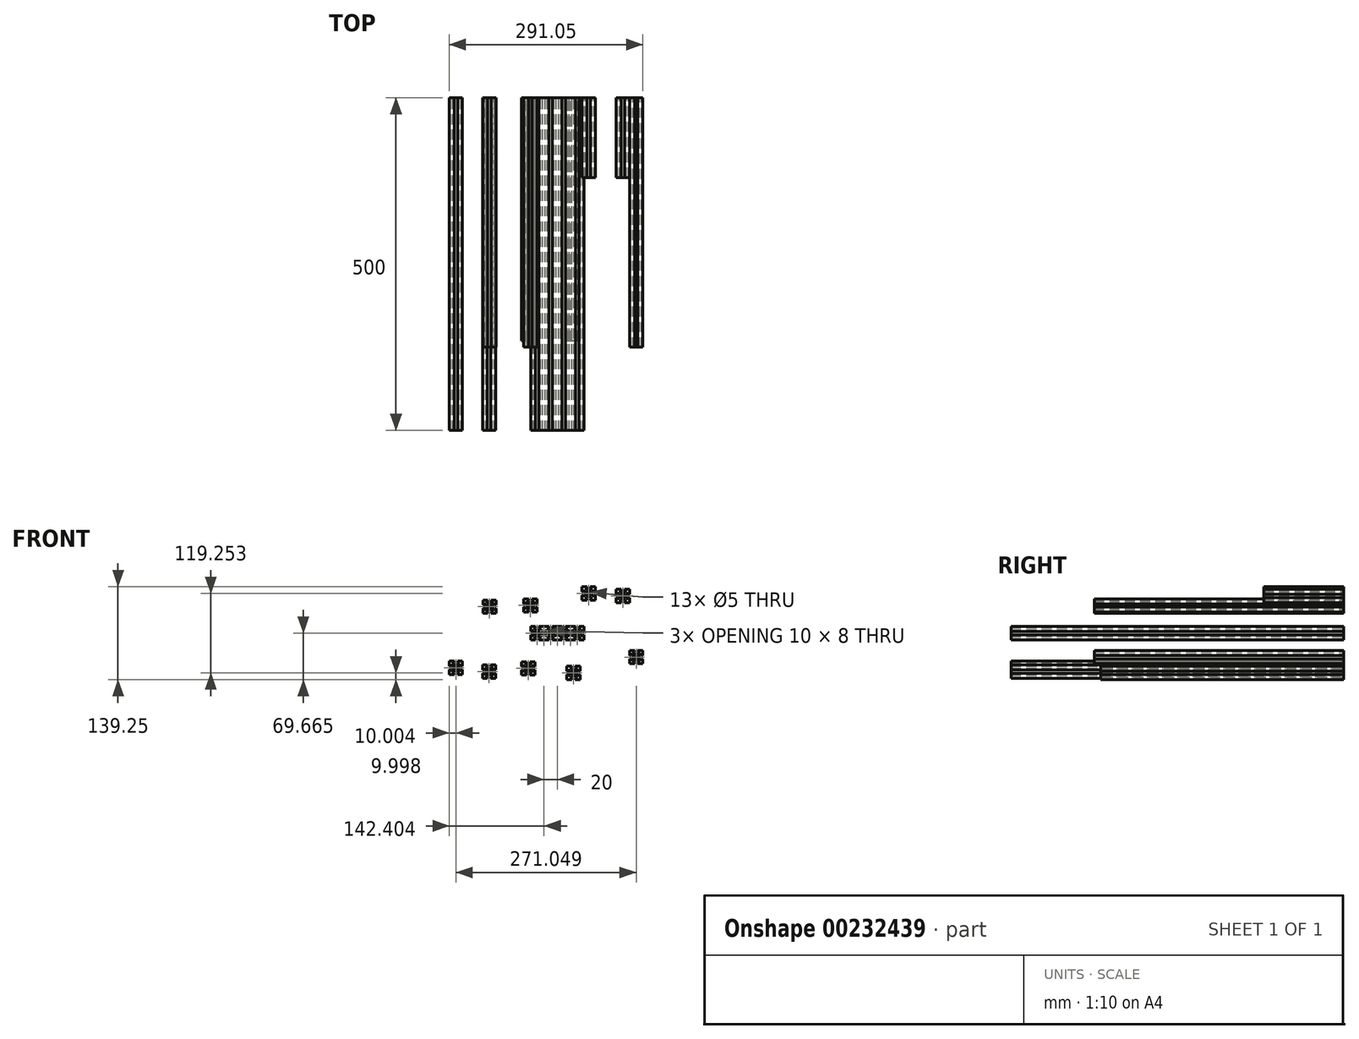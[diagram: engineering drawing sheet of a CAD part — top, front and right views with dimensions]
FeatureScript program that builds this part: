
annotation { "Feature Type Name" : "Feature", "Feature Type Description" : "" }
export const myFeature = defineFeature(function(context is Context, id is Id, definition is map)
    precondition{}
    {
        {
            var Q0;
            Q0=qCreatedBy(makeId("Front.planeOp"),FACE);
            var sketch = newSketch(context, id + "F0", { "sketchPlane" : qUnion([Q0])});
            skLineSegment(sketch, "E0.bottom", {"start": v(-60.37, 62.95) * mm, "end": v(-52.87, 62.95) * mm});
            skLineSegment(sketch, "E0.top", {"start": v(-60.37, 42.95) * mm, "end": v(-52.87, 42.95) * mm});
            skLineSegment(sketch, "E0.left", {"start": v(-60.37, 62.95) * mm, "end": v(-60.37, 55.45) * mm});
            skLineSegment(sketch, "E0.right", {"start": v(-40.37, 62.95) * mm, "end": v(-40.37, 55.45) * mm});
            skLineSegment(sketch, "E1.right", {"start": v(-47.87, 62.95) * mm, "end": v(-47.87, 60.95) * mm});
            skCircle(sketch, "E2", {"center": v(-50.37, 52.95) * mm, "radius": 2.5 * mm});
            skLineSegment(sketch, "E3.MirrorCS", {"start": v(-52.87, 62.95) * mm, "end": v(-52.87, 60.95) * mm});
            skLineSegment(sketch, "E4.bottom", {"start": v(-47.87, 60.95) * mm, "end": v(-46.37, 60.95) * mm});
            skLineSegment(sketch, "E4.top", {"start": v(-50.37, 57.95) * mm, "end": v(-46.37, 57.95) * mm});
            skLineSegment(sketch, "E4.right", {"start": v(-46.37, 60.95) * mm, "end": v(-46.37, 57.95) * mm});
            skLineSegment(sketch, "E5.MirrorCS", {"start": v(-54.37, 60.95) * mm, "end": v(-54.37, 57.95) * mm});
            skLineSegment(sketch, "E6.MirrorCS", {"start": v(-52.87, 60.95) * mm, "end": v(-54.37, 60.95) * mm});
            skLineSegment(sketch, "E7.MirrorCS", {"start": v(-50.37, 57.95) * mm, "end": v(-54.37, 57.95) * mm});
            skPoint(sketch, "E8.MirrorCS.end.orphan", {"position": v(-52.87, 60.95) * mm});
            skPoint(sketch, "E8.MirrorCS.start.orphan", {"position": v(-50.37, 60.95) * mm});
            skLineSegment(sketch, "E9.trimOffspring", {"start": v(-47.87, 62.95) * mm, "end": v(-40.37, 62.95) * mm});
            skPoint(sketch, "E1.bottom.start.orphan", {"position": v(-50.37, 62.95) * mm});
            skLineSegment(sketch, "E10.MirrorCS", {"start": v(-58.37, 55.45) * mm, "end": v(-58.37, 56.95) * mm});
            skLineSegment(sketch, "E11.MirrorCS", {"start": v(-55.37, 52.95) * mm, "end": v(-55.37, 56.95) * mm});
            skLineSegment(sketch, "E12.MirrorCS", {"start": v(-58.37, 48.95) * mm, "end": v(-55.37, 48.95) * mm});
            skLineSegment(sketch, "E13.MirrorCS", {"start": v(-55.37, 52.95) * mm, "end": v(-55.37, 48.95) * mm});
            skLineSegment(sketch, "E14.MirrorCS", {"start": v(-58.37, 50.45) * mm, "end": v(-58.37, 48.95) * mm});
            skLineSegment(sketch, "E15.MirrorCS", {"start": v(-58.37, 56.95) * mm, "end": v(-55.37, 56.95) * mm});
            skPoint(sketch, "E16.MirrorP", {"position": v(-58.37, 55.45) * mm});
            skPoint(sketch, "E17.MirrorP", {"position": v(-60.37, 52.95) * mm});
            skLineSegment(sketch, "E18.MirrorCS", {"start": v(-60.37, 55.45) * mm, "end": v(-58.37, 55.45) * mm});
            skLineSegment(sketch, "E19.MirrorCS", {"start": v(-60.37, 50.45) * mm, "end": v(-58.37, 50.45) * mm});
            skPoint(sketch, "E20.MirrorP", {"position": v(-58.37, 52.95) * mm});
            skPoint(sketch, "E21.orphan", {"position": v(-40.37, 62.95) * mm});
            skPoint(sketch, "E22.MirrorP", {"position": v(-40.37, 52.95) * mm});
            skLineSegment(sketch, "E23.MirrorCS", {"start": v(-42.37, 50.45) * mm, "end": v(-42.37, 48.95) * mm});
            skLineSegment(sketch, "E24.MirrorCS", {"start": v(-45.37, 52.95) * mm, "end": v(-45.37, 48.95) * mm});
            skLineSegment(sketch, "E25.MirrorCS", {"start": v(-40.37, 50.45) * mm, "end": v(-42.37, 50.45) * mm});
            skLineSegment(sketch, "E26.MirrorCS", {"start": v(-42.37, 55.45) * mm, "end": v(-42.37, 56.95) * mm});
            skLineSegment(sketch, "E27.MirrorCS", {"start": v(-45.37, 52.95) * mm, "end": v(-45.37, 56.95) * mm});
            skPoint(sketch, "E28.MirrorP", {"position": v(-42.37, 52.95) * mm});
            skLineSegment(sketch, "E29.MirrorCS", {"start": v(-42.37, 56.95) * mm, "end": v(-45.37, 56.95) * mm});
            skLineSegment(sketch, "E30.MirrorCS", {"start": v(-40.37, 55.45) * mm, "end": v(-42.37, 55.45) * mm});
            skLineSegment(sketch, "E31.MirrorCS", {"start": v(-42.37, 48.95) * mm, "end": v(-45.37, 48.95) * mm});
            skPoint(sketch, "E32.MirrorP", {"position": v(-42.37, 50.45) * mm});
            skLineSegment(sketch, "E33.MirrorCS", {"start": v(-47.87, 44.95) * mm, "end": v(-46.37, 44.95) * mm});
            skLineSegment(sketch, "E34.MirrorCS", {"start": v(-47.87, 42.95) * mm, "end": v(-47.87, 44.95) * mm});
            skLineSegment(sketch, "E35.MirrorCS", {"start": v(-52.87, 42.95) * mm, "end": v(-52.87, 44.95) * mm});
            skLineSegment(sketch, "E36.MirrorCS", {"start": v(-52.87, 44.95) * mm, "end": v(-54.37, 44.95) * mm});
            skLineSegment(sketch, "E37.MirrorCS", {"start": v(-54.37, 44.95) * mm, "end": v(-54.37, 47.95) * mm});
            skLineSegment(sketch, "E38.MirrorCS", {"start": v(-50.37, 47.95) * mm, "end": v(-54.37, 47.95) * mm});
            skLineSegment(sketch, "E39.MirrorCS", {"start": v(-46.37, 44.95) * mm, "end": v(-46.37, 47.95) * mm});
            skLineSegment(sketch, "E40.MirrorCS", {"start": v(-50.37, 47.95) * mm, "end": v(-46.37, 47.95) * mm});
            skLineSegment(sketch, "E41.trimOffspring", {"start": v(-40.37, 50.45) * mm, "end": v(-40.37, 42.95) * mm});
            skLineSegment(sketch, "E42.trimOffspring", {"start": v(-47.87, 42.95) * mm, "end": v(-40.37, 42.95) * mm});
            skLineSegment(sketch, "E43.trimOffspring", {"start": v(-60.37, 50.45) * mm, "end": v(-60.37, 42.95) * mm});
            skPoint(sketch, "E44.orphan", {"position": v(-60.37, 42.95) * mm});
            skLineSegment(sketch, "E45.bottom", {"start": v(1.09, 64.79) * mm, "end": v(8.59, 64.79) * mm});
            skLineSegment(sketch, "E45.top", {"start": v(1.09, 44.79) * mm, "end": v(8.59, 44.79) * mm});
            skLineSegment(sketch, "E45.left", {"start": v(1.09, 64.79) * mm, "end": v(1.09, 57.29) * mm});
            skLineSegment(sketch, "E45.right", {"start": v(21.09, 64.79) * mm, "end": v(21.09, 57.29) * mm});
            skLineSegment(sketch, "E46.right", {"start": v(13.59, 64.79) * mm, "end": v(13.59, 62.79) * mm});
            skCircle(sketch, "E47", {"center": v(11.09, 54.79) * mm, "radius": 2.5 * mm});
            skLineSegment(sketch, "E48.MirrorCS", {"start": v(8.59, 64.79) * mm, "end": v(8.59, 62.79) * mm});
            skLineSegment(sketch, "E49.bottom", {"start": v(13.59, 62.79) * mm, "end": v(15.09, 62.79) * mm});
            skLineSegment(sketch, "E49.top", {"start": v(11.09, 59.79) * mm, "end": v(15.09, 59.79) * mm});
            skLineSegment(sketch, "E49.right", {"start": v(15.09, 62.79) * mm, "end": v(15.09, 59.79) * mm});
            skLineSegment(sketch, "E50.MirrorCS", {"start": v(7.09, 62.79) * mm, "end": v(7.09, 59.79) * mm});
            skLineSegment(sketch, "E51.MirrorCS", {"start": v(8.59, 62.79) * mm, "end": v(7.09, 62.79) * mm});
            skLineSegment(sketch, "E52.MirrorCS", {"start": v(11.09, 59.79) * mm, "end": v(7.09, 59.79) * mm});
            skPoint(sketch, "E53.MirrorCS.end.orphan", {"position": v(8.59, 62.79) * mm});
            skPoint(sketch, "E53.MirrorCS.start.orphan", {"position": v(11.09, 62.79) * mm});
            skLineSegment(sketch, "E54.trimOffspring", {"start": v(13.59, 64.79) * mm, "end": v(21.09, 64.79) * mm});
            skPoint(sketch, "E46.bottom.start.orphan", {"position": v(11.09, 64.79) * mm});
            skLineSegment(sketch, "E55.MirrorCS", {"start": v(3.09, 57.29) * mm, "end": v(3.09, 58.79) * mm});
            skLineSegment(sketch, "E56.MirrorCS", {"start": v(6.09, 54.79) * mm, "end": v(6.09, 58.79) * mm});
            skLineSegment(sketch, "E57.MirrorCS", {"start": v(3.09, 50.79) * mm, "end": v(6.09, 50.79) * mm});
            skLineSegment(sketch, "E58.MirrorCS", {"start": v(6.09, 54.79) * mm, "end": v(6.09, 50.79) * mm});
            skLineSegment(sketch, "E59.MirrorCS", {"start": v(3.09, 52.29) * mm, "end": v(3.09, 50.79) * mm});
            skLineSegment(sketch, "E60.MirrorCS", {"start": v(3.09, 58.79) * mm, "end": v(6.09, 58.79) * mm});
            skPoint(sketch, "E61.MirrorP", {"position": v(3.09, 57.29) * mm});
            skPoint(sketch, "E62.MirrorP", {"position": v(1.09, 54.79) * mm});
            skLineSegment(sketch, "E63.MirrorCS", {"start": v(1.09, 57.29) * mm, "end": v(3.09, 57.29) * mm});
            skLineSegment(sketch, "E64.MirrorCS", {"start": v(1.09, 52.29) * mm, "end": v(3.09, 52.29) * mm});
            skPoint(sketch, "E65.MirrorP", {"position": v(3.09, 54.79) * mm});
            skPoint(sketch, "E66.orphan", {"position": v(21.09, 64.79) * mm});
            skPoint(sketch, "E67.MirrorP", {"position": v(21.09, 54.79) * mm});
            skLineSegment(sketch, "E68.MirrorCS", {"start": v(19.09, 52.29) * mm, "end": v(19.09, 50.79) * mm});
            skLineSegment(sketch, "E69.MirrorCS", {"start": v(16.09, 54.79) * mm, "end": v(16.09, 50.79) * mm});
            skLineSegment(sketch, "E70.MirrorCS", {"start": v(21.09, 52.29) * mm, "end": v(19.09, 52.29) * mm});
            skLineSegment(sketch, "E71.MirrorCS", {"start": v(19.09, 57.29) * mm, "end": v(19.09, 58.79) * mm});
            skLineSegment(sketch, "E72.MirrorCS", {"start": v(16.09, 54.79) * mm, "end": v(16.09, 58.79) * mm});
            skPoint(sketch, "E73.MirrorP", {"position": v(19.09, 54.79) * mm});
            skLineSegment(sketch, "E74.MirrorCS", {"start": v(19.09, 58.79) * mm, "end": v(16.09, 58.79) * mm});
            skLineSegment(sketch, "E75.MirrorCS", {"start": v(21.09, 57.29) * mm, "end": v(19.09, 57.29) * mm});
            skLineSegment(sketch, "E76.MirrorCS", {"start": v(19.09, 50.79) * mm, "end": v(16.09, 50.79) * mm});
            skPoint(sketch, "E77.MirrorP", {"position": v(19.09, 52.29) * mm});
            skLineSegment(sketch, "E78.MirrorCS", {"start": v(13.59, 46.79) * mm, "end": v(15.09, 46.79) * mm});
            skLineSegment(sketch, "E79.MirrorCS", {"start": v(13.59, 44.79) * mm, "end": v(13.59, 46.79) * mm});
            skLineSegment(sketch, "E80.MirrorCS", {"start": v(8.59, 44.79) * mm, "end": v(8.59, 46.79) * mm});
            skLineSegment(sketch, "E81.MirrorCS", {"start": v(8.59, 46.79) * mm, "end": v(7.09, 46.79) * mm});
            skLineSegment(sketch, "E82.MirrorCS", {"start": v(7.09, 46.79) * mm, "end": v(7.09, 49.79) * mm});
            skLineSegment(sketch, "E83.MirrorCS", {"start": v(11.09, 49.79) * mm, "end": v(7.09, 49.79) * mm});
            skLineSegment(sketch, "E84.MirrorCS", {"start": v(15.09, 46.79) * mm, "end": v(15.09, 49.79) * mm});
            skLineSegment(sketch, "E85.MirrorCS", {"start": v(11.09, 49.79) * mm, "end": v(15.09, 49.79) * mm});
            skLineSegment(sketch, "E86.trimOffspring", {"start": v(21.09, 52.29) * mm, "end": v(21.09, 44.79) * mm});
            skLineSegment(sketch, "E87.trimOffspring", {"start": v(13.59, 44.79) * mm, "end": v(21.09, 44.79) * mm});
            skLineSegment(sketch, "E88.trimOffspring", {"start": v(1.09, 52.29) * mm, "end": v(1.09, 44.79) * mm});
            skPoint(sketch, "E89.orphan", {"position": v(1.09, 44.79) * mm});
            skLineSegment(sketch, "E90.bottom", {"start": v(-47.85, -7.16) * mm, "end": v(-40.35, -7.16) * mm});
            skLineSegment(sketch, "E90.top", {"start": v(-47.85, -27.16) * mm, "end": v(-40.35, -27.16) * mm});
            skLineSegment(sketch, "E90.left", {"start": v(-47.85, -7.16) * mm, "end": v(-47.85, -14.66) * mm});
            skLineSegment(sketch, "E90.right", {"start": v(-27.85, -7.16) * mm, "end": v(-27.85, -14.66) * mm});
            skLineSegment(sketch, "E91.right", {"start": v(-35.35, -7.16) * mm, "end": v(-35.35, -9.16) * mm});
            skCircle(sketch, "E92", {"center": v(-37.85, -17.16) * mm, "radius": 2.5 * mm});
            skLineSegment(sketch, "E93.MirrorCS", {"start": v(-40.35, -7.16) * mm, "end": v(-40.35, -9.16) * mm});
            skLineSegment(sketch, "E94.bottom", {"start": v(-35.35, -9.16) * mm, "end": v(-33.85, -9.16) * mm});
            skLineSegment(sketch, "E94.top", {"start": v(-37.85, -12.16) * mm, "end": v(-33.85, -12.16) * mm});
            skLineSegment(sketch, "E94.right", {"start": v(-33.85, -9.16) * mm, "end": v(-33.85, -12.16) * mm});
            skLineSegment(sketch, "E95.MirrorCS", {"start": v(-41.85, -9.16) * mm, "end": v(-41.85, -12.16) * mm});
            skLineSegment(sketch, "E96.MirrorCS", {"start": v(-40.35, -9.16) * mm, "end": v(-41.85, -9.16) * mm});
            skLineSegment(sketch, "E97.MirrorCS", {"start": v(-37.85, -12.16) * mm, "end": v(-41.85, -12.16) * mm});
            skPoint(sketch, "E98.MirrorCS.end.orphan", {"position": v(-40.35, -9.16) * mm});
            skPoint(sketch, "E98.MirrorCS.start.orphan", {"position": v(-37.85, -9.16) * mm});
            skLineSegment(sketch, "E99.trimOffspring", {"start": v(-35.35, -7.16) * mm, "end": v(-27.85, -7.16) * mm});
            skPoint(sketch, "E91.bottom.start.orphan", {"position": v(-37.85, -7.16) * mm});
            skLineSegment(sketch, "E100.MirrorCS", {"start": v(-45.85, -14.66) * mm, "end": v(-45.85, -13.16) * mm});
            skLineSegment(sketch, "E101.MirrorCS", {"start": v(-42.85, -17.16) * mm, "end": v(-42.85, -13.16) * mm});
            skLineSegment(sketch, "E102.MirrorCS", {"start": v(-45.85, -21.16) * mm, "end": v(-42.85, -21.16) * mm});
            skLineSegment(sketch, "E103.MirrorCS", {"start": v(-42.85, -17.16) * mm, "end": v(-42.85, -21.16) * mm});
            skLineSegment(sketch, "E104.MirrorCS", {"start": v(-45.85, -19.66) * mm, "end": v(-45.85, -21.16) * mm});
            skLineSegment(sketch, "E105.MirrorCS", {"start": v(-45.85, -13.16) * mm, "end": v(-42.85, -13.16) * mm});
            skPoint(sketch, "E106.MirrorP", {"position": v(-45.85, -14.66) * mm});
            skPoint(sketch, "E107.MirrorP", {"position": v(-47.85, -17.16) * mm});
            skLineSegment(sketch, "E108.MirrorCS", {"start": v(-47.85, -14.66) * mm, "end": v(-45.85, -14.66) * mm});
            skLineSegment(sketch, "E109.MirrorCS", {"start": v(-47.85, -19.66) * mm, "end": v(-45.85, -19.66) * mm});
            skPoint(sketch, "E110.MirrorP", {"position": v(-45.85, -17.16) * mm});
            skPoint(sketch, "E111.orphan", {"position": v(-27.85, -7.16) * mm});
            skPoint(sketch, "E112.MirrorP", {"position": v(-27.85, -17.16) * mm});
            skLineSegment(sketch, "E113.MirrorCS", {"start": v(-29.85, -19.66) * mm, "end": v(-29.85, -21.16) * mm});
            skLineSegment(sketch, "E114.MirrorCS", {"start": v(-32.85, -17.16) * mm, "end": v(-32.85, -21.16) * mm});
            skLineSegment(sketch, "E115.MirrorCS", {"start": v(-27.85, -19.66) * mm, "end": v(-29.85, -19.66) * mm});
            skLineSegment(sketch, "E116.MirrorCS", {"start": v(-29.85, -14.66) * mm, "end": v(-29.85, -13.16) * mm});
            skLineSegment(sketch, "E117.MirrorCS", {"start": v(-32.85, -17.16) * mm, "end": v(-32.85, -13.16) * mm});
            skPoint(sketch, "E118.MirrorP", {"position": v(-29.85, -17.16) * mm});
            skLineSegment(sketch, "E119.MirrorCS", {"start": v(-29.85, -13.16) * mm, "end": v(-32.85, -13.16) * mm});
            skLineSegment(sketch, "E120.MirrorCS", {"start": v(-27.85, -14.66) * mm, "end": v(-29.85, -14.66) * mm});
            skLineSegment(sketch, "E121.MirrorCS", {"start": v(-29.85, -21.16) * mm, "end": v(-32.85, -21.16) * mm});
            skPoint(sketch, "E122.MirrorP", {"position": v(-29.85, -19.66) * mm});
            skLineSegment(sketch, "E123.MirrorCS", {"start": v(-35.35, -25.16) * mm, "end": v(-33.85, -25.16) * mm});
            skLineSegment(sketch, "E124.MirrorCS", {"start": v(-35.35, -27.16) * mm, "end": v(-35.35, -25.16) * mm});
            skLineSegment(sketch, "E125.MirrorCS", {"start": v(-40.35, -27.16) * mm, "end": v(-40.35, -25.16) * mm});
            skLineSegment(sketch, "E126.MirrorCS", {"start": v(-40.35, -25.16) * mm, "end": v(-41.85, -25.16) * mm});
            skLineSegment(sketch, "E127.MirrorCS", {"start": v(-41.85, -25.16) * mm, "end": v(-41.85, -22.16) * mm});
            skLineSegment(sketch, "E128.MirrorCS", {"start": v(-37.85, -22.16) * mm, "end": v(-41.85, -22.16) * mm});
            skLineSegment(sketch, "E129.MirrorCS", {"start": v(-33.85, -25.16) * mm, "end": v(-33.85, -22.16) * mm});
            skLineSegment(sketch, "E130.MirrorCS", {"start": v(-37.85, -22.16) * mm, "end": v(-33.85, -22.16) * mm});
            skLineSegment(sketch, "E131.trimOffspring", {"start": v(-27.85, -19.66) * mm, "end": v(-27.85, -27.16) * mm});
            skLineSegment(sketch, "E132.trimOffspring", {"start": v(-35.35, -27.16) * mm, "end": v(-27.85, -27.16) * mm});
            skLineSegment(sketch, "E133.trimOffspring", {"start": v(-47.85, -19.66) * mm, "end": v(-47.85, -27.16) * mm});
            skPoint(sketch, "E134.orphan", {"position": v(-47.85, -27.16) * mm});
            skLineSegment(sketch, "E135.bottom", {"start": v(36.99, -2) * mm, "end": v(44.49, -2) * mm});
            skLineSegment(sketch, "E135.top", {"start": v(36.99, -22) * mm, "end": v(44.49, -22) * mm});
            skLineSegment(sketch, "E135.left", {"start": v(36.99, -2) * mm, "end": v(36.99, -9.5) * mm});
            skLineSegment(sketch, "E135.right", {"start": v(56.99, -2) * mm, "end": v(56.99, -9.5) * mm});
            skLineSegment(sketch, "E136.right", {"start": v(49.49, -2) * mm, "end": v(49.49, -4) * mm});
            skCircle(sketch, "E137", {"center": v(46.99, -12) * mm, "radius": 2.5 * mm});
            skLineSegment(sketch, "E138.MirrorCS", {"start": v(44.49, -2) * mm, "end": v(44.49, -4) * mm});
            skLineSegment(sketch, "E139.bottom", {"start": v(49.49, -4) * mm, "end": v(50.99, -4) * mm});
            skLineSegment(sketch, "E139.top", {"start": v(46.99, -7) * mm, "end": v(50.99, -7) * mm});
            skLineSegment(sketch, "E139.right", {"start": v(50.99, -4) * mm, "end": v(50.99, -7) * mm});
            skLineSegment(sketch, "E140.MirrorCS", {"start": v(42.99, -4) * mm, "end": v(42.99, -7) * mm});
            skLineSegment(sketch, "E141.MirrorCS", {"start": v(44.49, -4) * mm, "end": v(42.99, -4) * mm});
            skLineSegment(sketch, "E142.MirrorCS", {"start": v(46.99, -7) * mm, "end": v(42.99, -7) * mm});
            skPoint(sketch, "E143.MirrorCS.end.orphan", {"position": v(44.49, -4) * mm});
            skPoint(sketch, "E143.MirrorCS.start.orphan", {"position": v(46.99, -4) * mm});
            skLineSegment(sketch, "E144.trimOffspring", {"start": v(49.49, -2) * mm, "end": v(56.99, -2) * mm});
            skPoint(sketch, "E136.bottom.start.orphan", {"position": v(46.99, -2) * mm});
            skLineSegment(sketch, "E145.MirrorCS", {"start": v(38.99, -9.5) * mm, "end": v(38.99, -8) * mm});
            skLineSegment(sketch, "E146.MirrorCS", {"start": v(41.99, -12) * mm, "end": v(41.99, -8) * mm});
            skLineSegment(sketch, "E147.MirrorCS", {"start": v(38.99, -16) * mm, "end": v(41.99, -16) * mm});
            skLineSegment(sketch, "E148.MirrorCS", {"start": v(41.99, -12) * mm, "end": v(41.99, -16) * mm});
            skLineSegment(sketch, "E149.MirrorCS", {"start": v(38.99, -14.5) * mm, "end": v(38.99, -16) * mm});
            skLineSegment(sketch, "E150.MirrorCS", {"start": v(38.99, -8) * mm, "end": v(41.99, -8) * mm});
            skPoint(sketch, "E151.MirrorP", {"position": v(38.99, -9.5) * mm});
            skPoint(sketch, "E152.MirrorP", {"position": v(36.99, -12) * mm});
            skLineSegment(sketch, "E153.MirrorCS", {"start": v(36.99, -9.5) * mm, "end": v(38.99, -9.5) * mm});
            skLineSegment(sketch, "E154.MirrorCS", {"start": v(36.99, -14.5) * mm, "end": v(38.99, -14.5) * mm});
            skPoint(sketch, "E155.MirrorP", {"position": v(38.99, -12) * mm});
            skPoint(sketch, "E156.orphan", {"position": v(56.99, -2) * mm});
            skPoint(sketch, "E157.MirrorP", {"position": v(56.99, -12) * mm});
            skLineSegment(sketch, "E158.MirrorCS", {"start": v(54.99, -14.5) * mm, "end": v(54.99, -16) * mm});
            skLineSegment(sketch, "E159.MirrorCS", {"start": v(51.99, -12) * mm, "end": v(51.99, -16) * mm});
            skLineSegment(sketch, "E160.MirrorCS", {"start": v(56.99, -14.5) * mm, "end": v(54.99, -14.5) * mm});
            skLineSegment(sketch, "E161.MirrorCS", {"start": v(54.99, -9.5) * mm, "end": v(54.99, -8) * mm});
            skLineSegment(sketch, "E162.MirrorCS", {"start": v(51.99, -12) * mm, "end": v(51.99, -8) * mm});
            skPoint(sketch, "E163.MirrorP", {"position": v(54.99, -12) * mm});
            skLineSegment(sketch, "E164.MirrorCS", {"start": v(54.99, -8) * mm, "end": v(51.99, -8) * mm});
            skLineSegment(sketch, "E165.MirrorCS", {"start": v(56.99, -9.5) * mm, "end": v(54.99, -9.5) * mm});
            skLineSegment(sketch, "E166.MirrorCS", {"start": v(54.99, -16) * mm, "end": v(51.99, -16) * mm});
            skPoint(sketch, "E167.MirrorP", {"position": v(54.99, -14.5) * mm});
            skLineSegment(sketch, "E168.MirrorCS", {"start": v(49.49, -20) * mm, "end": v(50.99, -20) * mm});
            skLineSegment(sketch, "E169.MirrorCS", {"start": v(49.49, -22) * mm, "end": v(49.49, -20) * mm});
            skLineSegment(sketch, "E170.MirrorCS", {"start": v(44.49, -22) * mm, "end": v(44.49, -20) * mm});
            skLineSegment(sketch, "E171.MirrorCS", {"start": v(44.49, -20) * mm, "end": v(42.99, -20) * mm});
            skLineSegment(sketch, "E172.MirrorCS", {"start": v(42.99, -20) * mm, "end": v(42.99, -17) * mm});
            skLineSegment(sketch, "E173.MirrorCS", {"start": v(46.99, -17) * mm, "end": v(42.99, -17) * mm});
            skLineSegment(sketch, "E174.MirrorCS", {"start": v(50.99, -20) * mm, "end": v(50.99, -17) * mm});
            skLineSegment(sketch, "E175.MirrorCS", {"start": v(46.99, -17) * mm, "end": v(50.99, -17) * mm});
            skLineSegment(sketch, "E176.trimOffspring", {"start": v(56.99, -14.5) * mm, "end": v(56.99, -22) * mm});
            skLineSegment(sketch, "E177.trimOffspring", {"start": v(49.49, -22) * mm, "end": v(56.99, -22) * mm});
            skLineSegment(sketch, "E178.trimOffspring", {"start": v(36.99, -14.5) * mm, "end": v(36.99, -22) * mm});
            skPoint(sketch, "E179.orphan", {"position": v(36.99, -22) * mm});
            skLineSegment(sketch, "E180.bottom", {"start": v(61.03, 62.56) * mm, "end": v(68.53, 62.56) * mm});
            skLineSegment(sketch, "E180.top", {"start": v(61.03, 42.56) * mm, "end": v(68.53, 42.56) * mm});
            skLineSegment(sketch, "E180.left", {"start": v(61.03, 62.56) * mm, "end": v(61.03, 55.06) * mm});
            skLineSegment(sketch, "E180.right", {"start": v(81.03, 62.56) * mm, "end": v(81.03, 55.06) * mm});
            skLineSegment(sketch, "E181.right", {"start": v(73.53, 62.56) * mm, "end": v(73.53, 60.56) * mm});
            skCircle(sketch, "E182", {"center": v(71.03, 52.56) * mm, "radius": 2.5 * mm});
            skLineSegment(sketch, "E183.MirrorCS", {"start": v(68.53, 62.56) * mm, "end": v(68.53, 60.56) * mm});
            skLineSegment(sketch, "E184.bottom", {"start": v(73.53, 60.56) * mm, "end": v(75.03, 60.56) * mm});
            skLineSegment(sketch, "E184.top", {"start": v(71.03, 57.56) * mm, "end": v(75.03, 57.56) * mm});
            skLineSegment(sketch, "E184.right", {"start": v(75.03, 60.56) * mm, "end": v(75.03, 57.56) * mm});
            skLineSegment(sketch, "E185.MirrorCS", {"start": v(67.03, 60.56) * mm, "end": v(67.03, 57.56) * mm});
            skLineSegment(sketch, "E186.MirrorCS", {"start": v(68.53, 60.56) * mm, "end": v(67.03, 60.56) * mm});
            skLineSegment(sketch, "E187.MirrorCS", {"start": v(71.03, 57.56) * mm, "end": v(67.03, 57.56) * mm});
            skPoint(sketch, "E188.MirrorCS.end.orphan", {"position": v(68.53, 60.56) * mm});
            skPoint(sketch, "E188.MirrorCS.start.orphan", {"position": v(71.03, 60.56) * mm});
            skLineSegment(sketch, "E189.trimOffspring", {"start": v(73.53, 62.56) * mm, "end": v(81.03, 62.56) * mm});
            skPoint(sketch, "E181.bottom.start.orphan", {"position": v(71.03, 62.56) * mm});
            skLineSegment(sketch, "E190.MirrorCS", {"start": v(63.03, 55.06) * mm, "end": v(63.03, 56.56) * mm});
            skLineSegment(sketch, "E191.MirrorCS", {"start": v(66.03, 52.56) * mm, "end": v(66.03, 56.56) * mm});
            skLineSegment(sketch, "E192.MirrorCS", {"start": v(63.03, 48.56) * mm, "end": v(66.03, 48.56) * mm});
            skLineSegment(sketch, "E193.MirrorCS", {"start": v(66.03, 52.56) * mm, "end": v(66.03, 48.56) * mm});
            skLineSegment(sketch, "E194.MirrorCS", {"start": v(63.03, 50.06) * mm, "end": v(63.03, 48.56) * mm});
            skLineSegment(sketch, "E195.MirrorCS", {"start": v(63.03, 56.56) * mm, "end": v(66.03, 56.56) * mm});
            skPoint(sketch, "E196.MirrorP", {"position": v(63.03, 55.06) * mm});
            skPoint(sketch, "E197.MirrorP", {"position": v(61.03, 52.56) * mm});
            skLineSegment(sketch, "E198.MirrorCS", {"start": v(61.03, 55.06) * mm, "end": v(63.03, 55.06) * mm});
            skLineSegment(sketch, "E199.MirrorCS", {"start": v(61.03, 50.06) * mm, "end": v(63.03, 50.06) * mm});
            skPoint(sketch, "E200.MirrorP", {"position": v(63.03, 52.56) * mm});
            skPoint(sketch, "E201.orphan", {"position": v(81.03, 62.56) * mm});
            skPoint(sketch, "E202.MirrorP", {"position": v(81.03, 52.56) * mm});
            skLineSegment(sketch, "E203.MirrorCS", {"start": v(79.03, 50.06) * mm, "end": v(79.03, 48.56) * mm});
            skLineSegment(sketch, "E204.MirrorCS", {"start": v(76.03, 52.56) * mm, "end": v(76.03, 48.56) * mm});
            skLineSegment(sketch, "E205.MirrorCS", {"start": v(81.03, 50.06) * mm, "end": v(79.03, 50.06) * mm});
            skLineSegment(sketch, "E206.MirrorCS", {"start": v(79.03, 55.06) * mm, "end": v(79.03, 56.56) * mm});
            skLineSegment(sketch, "E207.MirrorCS", {"start": v(76.03, 52.56) * mm, "end": v(76.03, 56.56) * mm});
            skPoint(sketch, "E208.MirrorP", {"position": v(79.03, 52.56) * mm});
            skLineSegment(sketch, "E209.MirrorCS", {"start": v(79.03, 56.56) * mm, "end": v(76.03, 56.56) * mm});
            skLineSegment(sketch, "E210.MirrorCS", {"start": v(81.03, 55.06) * mm, "end": v(79.03, 55.06) * mm});
            skLineSegment(sketch, "E211.MirrorCS", {"start": v(79.03, 48.56) * mm, "end": v(76.03, 48.56) * mm});
            skPoint(sketch, "E212.MirrorP", {"position": v(79.03, 50.06) * mm});
            skLineSegment(sketch, "E213.MirrorCS", {"start": v(73.53, 44.56) * mm, "end": v(75.03, 44.56) * mm});
            skLineSegment(sketch, "E214.MirrorCS", {"start": v(73.53, 42.56) * mm, "end": v(73.53, 44.56) * mm});
            skLineSegment(sketch, "E215.MirrorCS", {"start": v(68.53, 42.56) * mm, "end": v(68.53, 44.56) * mm});
            skLineSegment(sketch, "E216.MirrorCS", {"start": v(68.53, 44.56) * mm, "end": v(67.03, 44.56) * mm});
            skLineSegment(sketch, "E217.MirrorCS", {"start": v(67.03, 44.56) * mm, "end": v(67.03, 47.56) * mm});
            skLineSegment(sketch, "E218.MirrorCS", {"start": v(71.03, 47.56) * mm, "end": v(67.03, 47.56) * mm});
            skLineSegment(sketch, "E219.MirrorCS", {"start": v(75.03, 44.56) * mm, "end": v(75.03, 47.56) * mm});
            skLineSegment(sketch, "E220.MirrorCS", {"start": v(71.03, 47.56) * mm, "end": v(75.03, 47.56) * mm});
            skLineSegment(sketch, "E221.trimOffspring", {"start": v(81.03, 50.06) * mm, "end": v(81.03, 42.56) * mm});
            skLineSegment(sketch, "E222.trimOffspring", {"start": v(73.53, 42.56) * mm, "end": v(81.03, 42.56) * mm});
            skLineSegment(sketch, "E223.trimOffspring", {"start": v(61.03, 50.06) * mm, "end": v(61.03, 42.56) * mm});
            skPoint(sketch, "E224.orphan", {"position": v(61.03, 42.56) * mm});
            skLineSegment(sketch, "E225.bottom", {"start": v(130.89, 63.14) * mm, "end": v(138.39, 63.14) * mm});
            skLineSegment(sketch, "E225.top", {"start": v(130.89, 43.14) * mm, "end": v(138.39, 43.14) * mm});
            skLineSegment(sketch, "E225.left", {"start": v(130.89, 63.14) * mm, "end": v(130.89, 55.64) * mm});
            skLineSegment(sketch, "E225.right", {"start": v(150.89, 63.14) * mm, "end": v(150.89, 55.64) * mm});
            skLineSegment(sketch, "E226.right", {"start": v(143.39, 63.14) * mm, "end": v(143.39, 61.14) * mm});
            skCircle(sketch, "E227", {"center": v(140.89, 53.14) * mm, "radius": 2.5 * mm});
            skLineSegment(sketch, "E228.MirrorCS", {"start": v(138.39, 63.14) * mm, "end": v(138.39, 61.14) * mm});
            skLineSegment(sketch, "E229.bottom", {"start": v(143.39, 61.14) * mm, "end": v(144.89, 61.14) * mm});
            skLineSegment(sketch, "E229.top", {"start": v(140.89, 58.14) * mm, "end": v(144.89, 58.14) * mm});
            skLineSegment(sketch, "E229.right", {"start": v(144.89, 61.14) * mm, "end": v(144.89, 58.14) * mm});
            skLineSegment(sketch, "E230.MirrorCS", {"start": v(136.89, 61.14) * mm, "end": v(136.89, 58.14) * mm});
            skLineSegment(sketch, "E231.MirrorCS", {"start": v(138.39, 61.14) * mm, "end": v(136.89, 61.14) * mm});
            skLineSegment(sketch, "E232.MirrorCS", {"start": v(140.89, 58.14) * mm, "end": v(136.89, 58.14) * mm});
            skPoint(sketch, "E233.MirrorCS.end.orphan", {"position": v(138.39, 61.14) * mm});
            skPoint(sketch, "E233.MirrorCS.start.orphan", {"position": v(140.89, 61.14) * mm});
            skLineSegment(sketch, "E234.trimOffspring", {"start": v(143.39, 63.14) * mm, "end": v(150.89, 63.14) * mm});
            skPoint(sketch, "E226.bottom.start.orphan", {"position": v(140.89, 63.14) * mm});
            skLineSegment(sketch, "E235.MirrorCS", {"start": v(132.89, 55.64) * mm, "end": v(132.89, 57.14) * mm});
            skLineSegment(sketch, "E236.MirrorCS", {"start": v(135.89, 53.14) * mm, "end": v(135.89, 57.14) * mm});
            skLineSegment(sketch, "E237.MirrorCS", {"start": v(132.89, 49.14) * mm, "end": v(135.89, 49.14) * mm});
            skLineSegment(sketch, "E238.MirrorCS", {"start": v(135.89, 53.14) * mm, "end": v(135.89, 49.14) * mm});
            skLineSegment(sketch, "E239.MirrorCS", {"start": v(132.89, 50.64) * mm, "end": v(132.89, 49.14) * mm});
            skLineSegment(sketch, "E240.MirrorCS", {"start": v(132.89, 57.14) * mm, "end": v(135.89, 57.14) * mm});
            skPoint(sketch, "E241.MirrorP", {"position": v(132.89, 55.64) * mm});
            skPoint(sketch, "E242.MirrorP", {"position": v(130.89, 53.14) * mm});
            skLineSegment(sketch, "E243.MirrorCS", {"start": v(130.89, 55.64) * mm, "end": v(132.89, 55.64) * mm});
            skLineSegment(sketch, "E244.MirrorCS", {"start": v(130.89, 50.64) * mm, "end": v(132.89, 50.64) * mm});
            skPoint(sketch, "E245.MirrorP", {"position": v(132.89, 53.14) * mm});
            skPoint(sketch, "E246.orphan", {"position": v(150.89, 63.14) * mm});
            skPoint(sketch, "E247.MirrorP", {"position": v(150.89, 53.14) * mm});
            skLineSegment(sketch, "E248.MirrorCS", {"start": v(148.89, 50.64) * mm, "end": v(148.89, 49.14) * mm});
            skLineSegment(sketch, "E249.MirrorCS", {"start": v(145.89, 53.14) * mm, "end": v(145.89, 49.14) * mm});
            skLineSegment(sketch, "E250.MirrorCS", {"start": v(150.89, 50.64) * mm, "end": v(148.89, 50.64) * mm});
            skLineSegment(sketch, "E251.MirrorCS", {"start": v(148.89, 55.64) * mm, "end": v(148.89, 57.14) * mm});
            skLineSegment(sketch, "E252.MirrorCS", {"start": v(145.89, 53.14) * mm, "end": v(145.89, 57.14) * mm});
            skPoint(sketch, "E253.MirrorP", {"position": v(148.89, 53.14) * mm});
            skLineSegment(sketch, "E254.MirrorCS", {"start": v(148.89, 57.14) * mm, "end": v(145.89, 57.14) * mm});
            skLineSegment(sketch, "E255.MirrorCS", {"start": v(150.89, 55.64) * mm, "end": v(148.89, 55.64) * mm});
            skLineSegment(sketch, "E256.MirrorCS", {"start": v(148.89, 49.14) * mm, "end": v(145.89, 49.14) * mm});
            skPoint(sketch, "E257.MirrorP", {"position": v(148.89, 50.64) * mm});
            skLineSegment(sketch, "E258.MirrorCS", {"start": v(143.39, 45.14) * mm, "end": v(144.89, 45.14) * mm});
            skLineSegment(sketch, "E259.MirrorCS", {"start": v(143.39, 43.14) * mm, "end": v(143.39, 45.14) * mm});
            skLineSegment(sketch, "E260.MirrorCS", {"start": v(138.39, 43.14) * mm, "end": v(138.39, 45.14) * mm});
            skLineSegment(sketch, "E261.MirrorCS", {"start": v(138.39, 45.14) * mm, "end": v(136.89, 45.14) * mm});
            skLineSegment(sketch, "E262.MirrorCS", {"start": v(136.89, 45.14) * mm, "end": v(136.89, 48.14) * mm});
            skLineSegment(sketch, "E263.MirrorCS", {"start": v(140.89, 48.14) * mm, "end": v(136.89, 48.14) * mm});
            skLineSegment(sketch, "E264.MirrorCS", {"start": v(144.89, 45.14) * mm, "end": v(144.89, 48.14) * mm});
            skLineSegment(sketch, "E265.MirrorCS", {"start": v(140.89, 48.14) * mm, "end": v(144.89, 48.14) * mm});
            skLineSegment(sketch, "E266.trimOffspring", {"start": v(150.89, 50.64) * mm, "end": v(150.89, 43.14) * mm});
            skLineSegment(sketch, "E267.trimOffspring", {"start": v(143.39, 43.14) * mm, "end": v(150.89, 43.14) * mm});
            skLineSegment(sketch, "E268.trimOffspring", {"start": v(130.89, 50.64) * mm, "end": v(130.89, 43.14) * mm});
            skPoint(sketch, "E269.orphan", {"position": v(130.89, 43.14) * mm});
            skLineSegment(sketch, "E270.bottom", {"start": v(85.34, -5.7) * mm, "end": v(92.84, -5.7) * mm});
            skLineSegment(sketch, "E270.top", {"start": v(85.34, -25.7) * mm, "end": v(92.84, -25.7) * mm});
            skLineSegment(sketch, "E270.left", {"start": v(85.34, -5.7) * mm, "end": v(85.34, -13.2) * mm});
            skLineSegment(sketch, "E270.right", {"start": v(105.34, -5.7) * mm, "end": v(105.34, -13.2) * mm});
            skLineSegment(sketch, "E271.right", {"start": v(97.84, -5.7) * mm, "end": v(97.84, -7.7) * mm});
            skCircle(sketch, "E272", {"center": v(95.34, -15.7) * mm, "radius": 2.5 * mm});
            skLineSegment(sketch, "E273.MirrorCS", {"start": v(92.84, -5.7) * mm, "end": v(92.84, -7.7) * mm});
            skLineSegment(sketch, "E274.bottom", {"start": v(97.84, -7.7) * mm, "end": v(99.34, -7.7) * mm});
            skLineSegment(sketch, "E274.top", {"start": v(95.34, -10.7) * mm, "end": v(99.34, -10.7) * mm});
            skLineSegment(sketch, "E274.right", {"start": v(99.34, -7.7) * mm, "end": v(99.34, -10.7) * mm});
            skLineSegment(sketch, "E275.MirrorCS", {"start": v(91.34, -7.7) * mm, "end": v(91.34, -10.7) * mm});
            skLineSegment(sketch, "E276.MirrorCS", {"start": v(92.84, -7.7) * mm, "end": v(91.34, -7.7) * mm});
            skLineSegment(sketch, "E277.MirrorCS", {"start": v(95.34, -10.7) * mm, "end": v(91.34, -10.7) * mm});
            skPoint(sketch, "E278.MirrorCS.end.orphan", {"position": v(92.84, -7.7) * mm});
            skPoint(sketch, "E278.MirrorCS.start.orphan", {"position": v(95.34, -7.7) * mm});
            skLineSegment(sketch, "E279.trimOffspring", {"start": v(97.84, -5.7) * mm, "end": v(105.34, -5.7) * mm});
            skPoint(sketch, "E271.bottom.start.orphan", {"position": v(95.34, -5.7) * mm});
            skLineSegment(sketch, "E280.MirrorCS", {"start": v(87.34, -13.2) * mm, "end": v(87.34, -11.7) * mm});
            skLineSegment(sketch, "E281.MirrorCS", {"start": v(90.34, -15.7) * mm, "end": v(90.34, -11.7) * mm});
            skLineSegment(sketch, "E282.MirrorCS", {"start": v(87.34, -19.7) * mm, "end": v(90.34, -19.7) * mm});
            skLineSegment(sketch, "E283.MirrorCS", {"start": v(90.34, -15.7) * mm, "end": v(90.34, -19.7) * mm});
            skLineSegment(sketch, "E284.MirrorCS", {"start": v(87.34, -18.2) * mm, "end": v(87.34, -19.7) * mm});
            skLineSegment(sketch, "E285.MirrorCS", {"start": v(87.34, -11.7) * mm, "end": v(90.34, -11.7) * mm});
            skPoint(sketch, "E286.MirrorP", {"position": v(87.34, -13.2) * mm});
            skPoint(sketch, "E287.MirrorP", {"position": v(85.34, -15.7) * mm});
            skLineSegment(sketch, "E288.MirrorCS", {"start": v(85.34, -13.2) * mm, "end": v(87.34, -13.2) * mm});
            skLineSegment(sketch, "E289.MirrorCS", {"start": v(85.34, -18.2) * mm, "end": v(87.34, -18.2) * mm});
            skPoint(sketch, "E290.MirrorP", {"position": v(87.34, -15.7) * mm});
            skPoint(sketch, "E291.orphan", {"position": v(105.34, -5.7) * mm});
            skPoint(sketch, "E292.MirrorP", {"position": v(105.34, -15.7) * mm});
            skLineSegment(sketch, "E293.MirrorCS", {"start": v(103.34, -18.2) * mm, "end": v(103.34, -19.7) * mm});
            skLineSegment(sketch, "E294.MirrorCS", {"start": v(100.34, -15.7) * mm, "end": v(100.34, -19.7) * mm});
            skLineSegment(sketch, "E295.MirrorCS", {"start": v(105.34, -18.2) * mm, "end": v(103.34, -18.2) * mm});
            skLineSegment(sketch, "E296.MirrorCS", {"start": v(103.34, -13.2) * mm, "end": v(103.34, -11.7) * mm});
            skLineSegment(sketch, "E297.MirrorCS", {"start": v(100.34, -15.7) * mm, "end": v(100.34, -11.7) * mm});
            skPoint(sketch, "E298.MirrorP", {"position": v(103.34, -15.7) * mm});
            skLineSegment(sketch, "E299.MirrorCS", {"start": v(103.34, -11.7) * mm, "end": v(100.34, -11.7) * mm});
            skLineSegment(sketch, "E300.MirrorCS", {"start": v(105.34, -13.2) * mm, "end": v(103.34, -13.2) * mm});
            skLineSegment(sketch, "E301.MirrorCS", {"start": v(103.34, -19.7) * mm, "end": v(100.34, -19.7) * mm});
            skPoint(sketch, "E302.MirrorP", {"position": v(103.34, -18.2) * mm});
            skLineSegment(sketch, "E303.MirrorCS", {"start": v(97.84, -23.7) * mm, "end": v(99.34, -23.7) * mm});
            skLineSegment(sketch, "E304.MirrorCS", {"start": v(97.84, -25.7) * mm, "end": v(97.84, -23.7) * mm});
            skLineSegment(sketch, "E305.MirrorCS", {"start": v(92.84, -25.7) * mm, "end": v(92.84, -23.7) * mm});
            skLineSegment(sketch, "E306.MirrorCS", {"start": v(92.84, -23.7) * mm, "end": v(91.34, -23.7) * mm});
            skLineSegment(sketch, "E307.MirrorCS", {"start": v(91.34, -23.7) * mm, "end": v(91.34, -20.7) * mm});
            skLineSegment(sketch, "E308.MirrorCS", {"start": v(95.34, -20.7) * mm, "end": v(91.34, -20.7) * mm});
            skLineSegment(sketch, "E309.MirrorCS", {"start": v(99.34, -23.7) * mm, "end": v(99.34, -20.7) * mm});
            skLineSegment(sketch, "E310.MirrorCS", {"start": v(95.34, -20.7) * mm, "end": v(99.34, -20.7) * mm});
            skLineSegment(sketch, "E311.trimOffspring", {"start": v(105.34, -18.2) * mm, "end": v(105.34, -25.7) * mm});
            skLineSegment(sketch, "E312.trimOffspring", {"start": v(97.84, -25.7) * mm, "end": v(105.34, -25.7) * mm});
            skLineSegment(sketch, "E313.trimOffspring", {"start": v(85.34, -18.2) * mm, "end": v(85.34, -25.7) * mm});
            skPoint(sketch, "E314.orphan", {"position": v(85.34, -25.7) * mm});
            skLineSegment(sketch, "E315.bottom", {"start": v(144.7, -6.69) * mm, "end": v(152.2, -6.69) * mm});
            skLineSegment(sketch, "E315.top", {"start": v(144.7, -26.69) * mm, "end": v(152.2, -26.69) * mm});
            skLineSegment(sketch, "E315.left", {"start": v(144.7, -6.69) * mm, "end": v(144.7, -14.19) * mm});
            skLineSegment(sketch, "E315.right", {"start": v(164.7, -6.69) * mm, "end": v(164.7, -14.19) * mm});
            skLineSegment(sketch, "E316.right", {"start": v(157.2, -6.69) * mm, "end": v(157.2, -8.69) * mm});
            skCircle(sketch, "E317", {"center": v(154.7, -16.69) * mm, "radius": 2.5 * mm});
            skLineSegment(sketch, "E318.MirrorCS", {"start": v(152.2, -6.69) * mm, "end": v(152.2, -8.69) * mm});
            skLineSegment(sketch, "E319.bottom", {"start": v(157.2, -8.69) * mm, "end": v(158.7, -8.69) * mm});
            skLineSegment(sketch, "E319.top", {"start": v(154.7, -11.69) * mm, "end": v(158.7, -11.69) * mm});
            skLineSegment(sketch, "E319.right", {"start": v(158.7, -8.69) * mm, "end": v(158.7, -11.69) * mm});
            skLineSegment(sketch, "E320.MirrorCS", {"start": v(150.7, -8.69) * mm, "end": v(150.7, -11.69) * mm});
            skLineSegment(sketch, "E321.MirrorCS", {"start": v(152.2, -8.69) * mm, "end": v(150.7, -8.69) * mm});
            skLineSegment(sketch, "E322.MirrorCS", {"start": v(154.7, -11.69) * mm, "end": v(150.7, -11.69) * mm});
            skPoint(sketch, "E323.MirrorCS.end.orphan", {"position": v(152.2, -8.69) * mm});
            skPoint(sketch, "E323.MirrorCS.start.orphan", {"position": v(154.7, -8.69) * mm});
            skLineSegment(sketch, "E324.trimOffspring", {"start": v(157.2, -6.69) * mm, "end": v(164.7, -6.69) * mm});
            skPoint(sketch, "E316.bottom.start.orphan", {"position": v(154.7, -6.69) * mm});
            skLineSegment(sketch, "E325.MirrorCS", {"start": v(146.7, -14.19) * mm, "end": v(146.7, -12.69) * mm});
            skLineSegment(sketch, "E326.MirrorCS", {"start": v(149.7, -16.69) * mm, "end": v(149.7, -12.69) * mm});
            skLineSegment(sketch, "E327.MirrorCS", {"start": v(146.7, -20.69) * mm, "end": v(149.7, -20.69) * mm});
            skLineSegment(sketch, "E328.MirrorCS", {"start": v(149.7, -16.69) * mm, "end": v(149.7, -20.69) * mm});
            skLineSegment(sketch, "E329.MirrorCS", {"start": v(146.7, -19.19) * mm, "end": v(146.7, -20.69) * mm});
            skLineSegment(sketch, "E330.MirrorCS", {"start": v(146.7, -12.69) * mm, "end": v(149.7, -12.69) * mm});
            skPoint(sketch, "E331.MirrorP", {"position": v(146.7, -14.19) * mm});
            skPoint(sketch, "E332.MirrorP", {"position": v(144.7, -16.69) * mm});
            skLineSegment(sketch, "E333.MirrorCS", {"start": v(144.7, -14.19) * mm, "end": v(146.7, -14.19) * mm});
            skLineSegment(sketch, "E334.MirrorCS", {"start": v(144.7, -19.19) * mm, "end": v(146.7, -19.19) * mm});
            skPoint(sketch, "E335.MirrorP", {"position": v(146.7, -16.69) * mm});
            skPoint(sketch, "E336.orphan", {"position": v(164.7, -6.69) * mm});
            skPoint(sketch, "E337.MirrorP", {"position": v(164.7, -16.69) * mm});
            skLineSegment(sketch, "E338.MirrorCS", {"start": v(162.7, -19.19) * mm, "end": v(162.7, -20.69) * mm});
            skLineSegment(sketch, "E339.MirrorCS", {"start": v(159.7, -16.69) * mm, "end": v(159.7, -20.69) * mm});
            skLineSegment(sketch, "E340.MirrorCS", {"start": v(164.7, -19.19) * mm, "end": v(162.7, -19.19) * mm});
            skLineSegment(sketch, "E341.MirrorCS", {"start": v(162.7, -14.19) * mm, "end": v(162.7, -12.69) * mm});
            skLineSegment(sketch, "E342.MirrorCS", {"start": v(159.7, -16.69) * mm, "end": v(159.7, -12.69) * mm});
            skPoint(sketch, "E343.MirrorP", {"position": v(162.7, -16.69) * mm});
            skLineSegment(sketch, "E344.MirrorCS", {"start": v(162.7, -12.69) * mm, "end": v(159.7, -12.69) * mm});
            skLineSegment(sketch, "E345.MirrorCS", {"start": v(164.7, -14.19) * mm, "end": v(162.7, -14.19) * mm});
            skLineSegment(sketch, "E346.MirrorCS", {"start": v(162.7, -20.69) * mm, "end": v(159.7, -20.69) * mm});
            skPoint(sketch, "E347.MirrorP", {"position": v(162.7, -19.19) * mm});
            skLineSegment(sketch, "E348.MirrorCS", {"start": v(157.2, -24.69) * mm, "end": v(158.7, -24.69) * mm});
            skLineSegment(sketch, "E349.MirrorCS", {"start": v(157.2, -26.69) * mm, "end": v(157.2, -24.69) * mm});
            skLineSegment(sketch, "E350.MirrorCS", {"start": v(152.2, -26.69) * mm, "end": v(152.2, -24.69) * mm});
            skLineSegment(sketch, "E351.MirrorCS", {"start": v(152.2, -24.69) * mm, "end": v(150.7, -24.69) * mm});
            skLineSegment(sketch, "E352.MirrorCS", {"start": v(150.7, -24.69) * mm, "end": v(150.7, -21.69) * mm});
            skLineSegment(sketch, "E353.MirrorCS", {"start": v(154.7, -21.69) * mm, "end": v(150.7, -21.69) * mm});
            skLineSegment(sketch, "E354.MirrorCS", {"start": v(158.7, -24.69) * mm, "end": v(158.7, -21.69) * mm});
            skLineSegment(sketch, "E355.MirrorCS", {"start": v(154.7, -21.69) * mm, "end": v(158.7, -21.69) * mm});
            skLineSegment(sketch, "E356.trimOffspring", {"start": v(164.7, -19.19) * mm, "end": v(164.7, -26.69) * mm});
            skLineSegment(sketch, "E357.trimOffspring", {"start": v(157.2, -26.69) * mm, "end": v(164.7, -26.69) * mm});
            skLineSegment(sketch, "E358.trimOffspring", {"start": v(144.7, -19.19) * mm, "end": v(144.7, -26.69) * mm});
            skPoint(sketch, "E359.orphan", {"position": v(144.7, -26.69) * mm});
            skSolve(sketch);
        }
        {
            var Q0;
            Q0=makeQuery(id+"F0.imprint","IMPRINT",FACE,{"disambiguationData":[TD([[makeQuery(id+"F0.imprint","IMPRINT",EDGE,{"derivedFrom":sQuery(id+"F0.wireOp",EDGE,"E0.bottom")}),-1.0]])]});
            var Q1;
            Q1=makeQuery(id+"F0.imprint","IMPRINT",FACE,{"disambiguationData":[TD([[makeQuery(id+"F0.imprint","IMPRINT",EDGE,{"derivedFrom":sQuery(id+"F0.wireOp",EDGE,"E45.bottom")}),-1.0]])]});
            extrude(context, id + "F1", {"entities" : qUnion([Q0, Q1]), "depth" : 375 * mm});
        }
        {
            var Q0;
            Q0=qCreatedBy(makeId("Front.planeOp"),FACE);
            var sketch = newSketch(context, id + "F2", { "sketchPlane" : qUnion([Q0])});
            skLineSegment(sketch, "E360.bottom", {"start": v(-2.17, -29.76) * mm, "end": v(5.33, -29.76) * mm});
            skLineSegment(sketch, "E360.top", {"start": v(-2.17, -49.76) * mm, "end": v(5.33, -49.76) * mm});
            skLineSegment(sketch, "E360.left", {"start": v(-2.17, -29.76) * mm, "end": v(-2.17, -37.26) * mm});
            skLineSegment(sketch, "E360.right", {"start": v(17.83, -29.76) * mm, "end": v(17.83, -37.26) * mm});
            skLineSegment(sketch, "E361.right", {"start": v(10.33, -29.76) * mm, "end": v(10.33, -31.76) * mm});
            skCircle(sketch, "E362", {"center": v(7.83, -39.76) * mm, "radius": 2.5 * mm});
            skLineSegment(sketch, "E363.MirrorCS", {"start": v(5.33, -29.76) * mm, "end": v(5.33, -31.76) * mm});
            skLineSegment(sketch, "E364.bottom", {"start": v(10.33, -31.76) * mm, "end": v(11.83, -31.76) * mm});
            skLineSegment(sketch, "E364.top", {"start": v(7.83, -34.76) * mm, "end": v(11.83, -34.76) * mm});
            skLineSegment(sketch, "E364.right", {"start": v(11.83, -31.76) * mm, "end": v(11.83, -34.76) * mm});
            skLineSegment(sketch, "E365.MirrorCS", {"start": v(3.83, -31.76) * mm, "end": v(3.83, -34.76) * mm});
            skLineSegment(sketch, "E366.MirrorCS", {"start": v(5.33, -31.76) * mm, "end": v(3.83, -31.76) * mm});
            skLineSegment(sketch, "E367.MirrorCS", {"start": v(7.83, -34.76) * mm, "end": v(3.83, -34.76) * mm});
            skPoint(sketch, "E368.MirrorCS.end.orphan", {"position": v(5.33, -31.76) * mm});
            skPoint(sketch, "E368.MirrorCS.start.orphan", {"position": v(7.83, -31.76) * mm});
            skLineSegment(sketch, "E369.trimOffspring", {"start": v(10.33, -29.76) * mm, "end": v(17.83, -29.76) * mm});
            skPoint(sketch, "E361.bottom.start.orphan", {"position": v(7.83, -29.76) * mm});
            skLineSegment(sketch, "E370.MirrorCS", {"start": v(-0.17, -37.26) * mm, "end": v(-0.17, -35.76) * mm});
            skLineSegment(sketch, "E371.MirrorCS", {"start": v(2.83, -39.76) * mm, "end": v(2.83, -35.76) * mm});
            skLineSegment(sketch, "E372.MirrorCS", {"start": v(-0.17, -43.76) * mm, "end": v(2.83, -43.76) * mm});
            skLineSegment(sketch, "E373.MirrorCS", {"start": v(2.83, -39.76) * mm, "end": v(2.83, -43.76) * mm});
            skLineSegment(sketch, "E374.MirrorCS", {"start": v(-0.17, -42.26) * mm, "end": v(-0.17, -43.76) * mm});
            skLineSegment(sketch, "E375.MirrorCS", {"start": v(-0.17, -35.76) * mm, "end": v(2.83, -35.76) * mm});
            skPoint(sketch, "E376.MirrorP", {"position": v(-0.17, -37.26) * mm});
            skPoint(sketch, "E377.MirrorP", {"position": v(-2.17, -39.76) * mm});
            skLineSegment(sketch, "E378.MirrorCS", {"start": v(-2.17, -37.26) * mm, "end": v(-0.17, -37.26) * mm});
            skLineSegment(sketch, "E379.MirrorCS", {"start": v(-2.17, -42.26) * mm, "end": v(-0.17, -42.26) * mm});
            skPoint(sketch, "E380.MirrorP", {"position": v(-0.17, -39.76) * mm});
            skPoint(sketch, "E381.orphan", {"position": v(17.83, -29.76) * mm});
            skPoint(sketch, "E382.MirrorP", {"position": v(17.83, -39.76) * mm});
            skLineSegment(sketch, "E383.MirrorCS", {"start": v(15.83, -42.26) * mm, "end": v(15.83, -43.76) * mm});
            skLineSegment(sketch, "E384.MirrorCS", {"start": v(12.83, -39.76) * mm, "end": v(12.83, -43.76) * mm});
            skLineSegment(sketch, "E385.MirrorCS", {"start": v(17.83, -42.26) * mm, "end": v(15.83, -42.26) * mm});
            skLineSegment(sketch, "E386.MirrorCS", {"start": v(15.83, -37.26) * mm, "end": v(15.83, -35.76) * mm});
            skLineSegment(sketch, "E387.MirrorCS", {"start": v(12.83, -39.76) * mm, "end": v(12.83, -35.76) * mm});
            skPoint(sketch, "E388.MirrorP", {"position": v(15.83, -39.76) * mm});
            skLineSegment(sketch, "E389.MirrorCS", {"start": v(15.83, -35.76) * mm, "end": v(12.83, -35.76) * mm});
            skLineSegment(sketch, "E390.MirrorCS", {"start": v(17.83, -37.26) * mm, "end": v(15.83, -37.26) * mm});
            skLineSegment(sketch, "E391.MirrorCS", {"start": v(15.83, -43.76) * mm, "end": v(12.83, -43.76) * mm});
            skPoint(sketch, "E392.MirrorP", {"position": v(15.83, -42.26) * mm});
            skLineSegment(sketch, "E393.MirrorCS", {"start": v(10.33, -47.76) * mm, "end": v(11.83, -47.76) * mm});
            skLineSegment(sketch, "E394.MirrorCS", {"start": v(10.33, -49.76) * mm, "end": v(10.33, -47.76) * mm});
            skLineSegment(sketch, "E395.MirrorCS", {"start": v(5.33, -49.76) * mm, "end": v(5.33, -47.76) * mm});
            skLineSegment(sketch, "E396.MirrorCS", {"start": v(5.33, -47.76) * mm, "end": v(3.83, -47.76) * mm});
            skLineSegment(sketch, "E397.MirrorCS", {"start": v(3.83, -47.76) * mm, "end": v(3.83, -44.76) * mm});
            skLineSegment(sketch, "E398.MirrorCS", {"start": v(7.83, -44.76) * mm, "end": v(3.83, -44.76) * mm});
            skLineSegment(sketch, "E399.MirrorCS", {"start": v(11.83, -47.76) * mm, "end": v(11.83, -44.76) * mm});
            skLineSegment(sketch, "E400.MirrorCS", {"start": v(7.83, -44.76) * mm, "end": v(11.83, -44.76) * mm});
            skLineSegment(sketch, "E401.trimOffspring", {"start": v(17.83, -42.26) * mm, "end": v(17.83, -49.76) * mm});
            skLineSegment(sketch, "E402.trimOffspring", {"start": v(10.33, -49.76) * mm, "end": v(17.83, -49.76) * mm});
            skLineSegment(sketch, "E403.trimOffspring", {"start": v(-2.17, -42.26) * mm, "end": v(-2.17, -49.76) * mm});
            skPoint(sketch, "E404.orphan", {"position": v(-2.17, -49.76) * mm});
            skLineSegment(sketch, "E405.bottom", {"start": v(65.95, -36.47) * mm, "end": v(73.45, -36.47) * mm});
            skLineSegment(sketch, "E405.top", {"start": v(65.95, -56.47) * mm, "end": v(73.45, -56.47) * mm});
            skLineSegment(sketch, "E405.left", {"start": v(65.95, -36.47) * mm, "end": v(65.95, -43.97) * mm});
            skLineSegment(sketch, "E405.right", {"start": v(85.95, -36.47) * mm, "end": v(85.95, -43.97) * mm});
            skLineSegment(sketch, "E406.right", {"start": v(78.45, -36.47) * mm, "end": v(78.45, -38.47) * mm});
            skCircle(sketch, "E407", {"center": v(75.95, -46.47) * mm, "radius": 2.5 * mm});
            skLineSegment(sketch, "E408.MirrorCS", {"start": v(73.45, -36.47) * mm, "end": v(73.45, -38.47) * mm});
            skLineSegment(sketch, "E409.bottom", {"start": v(78.45, -38.47) * mm, "end": v(79.95, -38.47) * mm});
            skLineSegment(sketch, "E409.top", {"start": v(75.95, -41.47) * mm, "end": v(79.95, -41.47) * mm});
            skLineSegment(sketch, "E409.right", {"start": v(79.95, -38.47) * mm, "end": v(79.95, -41.47) * mm});
            skLineSegment(sketch, "E410.MirrorCS", {"start": v(71.95, -38.47) * mm, "end": v(71.95, -41.47) * mm});
            skLineSegment(sketch, "E411.MirrorCS", {"start": v(73.45, -38.47) * mm, "end": v(71.95, -38.47) * mm});
            skLineSegment(sketch, "E412.MirrorCS", {"start": v(75.95, -41.47) * mm, "end": v(71.95, -41.47) * mm});
            skPoint(sketch, "E413.MirrorCS.end.orphan", {"position": v(73.45, -38.47) * mm});
            skPoint(sketch, "E413.MirrorCS.start.orphan", {"position": v(75.95, -38.47) * mm});
            skLineSegment(sketch, "E414.trimOffspring", {"start": v(78.45, -36.47) * mm, "end": v(85.95, -36.47) * mm});
            skPoint(sketch, "E406.bottom.start.orphan", {"position": v(75.95, -36.47) * mm});
            skLineSegment(sketch, "E415.MirrorCS", {"start": v(67.95, -43.97) * mm, "end": v(67.95, -42.47) * mm});
            skLineSegment(sketch, "E416.MirrorCS", {"start": v(70.95, -46.47) * mm, "end": v(70.95, -42.47) * mm});
            skLineSegment(sketch, "E417.MirrorCS", {"start": v(67.95, -50.47) * mm, "end": v(70.95, -50.47) * mm});
            skLineSegment(sketch, "E418.MirrorCS", {"start": v(70.95, -46.47) * mm, "end": v(70.95, -50.47) * mm});
            skLineSegment(sketch, "E419.MirrorCS", {"start": v(67.95, -48.97) * mm, "end": v(67.95, -50.47) * mm});
            skLineSegment(sketch, "E420.MirrorCS", {"start": v(67.95, -42.47) * mm, "end": v(70.95, -42.47) * mm});
            skPoint(sketch, "E421.MirrorP", {"position": v(67.95, -43.97) * mm});
            skPoint(sketch, "E422.MirrorP", {"position": v(65.95, -46.47) * mm});
            skLineSegment(sketch, "E423.MirrorCS", {"start": v(65.95, -43.97) * mm, "end": v(67.95, -43.97) * mm});
            skLineSegment(sketch, "E424.MirrorCS", {"start": v(65.95, -48.97) * mm, "end": v(67.95, -48.97) * mm});
            skPoint(sketch, "E425.MirrorP", {"position": v(67.95, -46.47) * mm});
            skPoint(sketch, "E426.orphan", {"position": v(85.95, -36.47) * mm});
            skPoint(sketch, "E427.MirrorP", {"position": v(85.95, -46.47) * mm});
            skLineSegment(sketch, "E428.MirrorCS", {"start": v(83.95, -48.97) * mm, "end": v(83.95, -50.47) * mm});
            skLineSegment(sketch, "E429.MirrorCS", {"start": v(80.95, -46.47) * mm, "end": v(80.95, -50.47) * mm});
            skLineSegment(sketch, "E430.MirrorCS", {"start": v(85.95, -48.97) * mm, "end": v(83.95, -48.97) * mm});
            skLineSegment(sketch, "E431.MirrorCS", {"start": v(83.95, -43.97) * mm, "end": v(83.95, -42.47) * mm});
            skLineSegment(sketch, "E432.MirrorCS", {"start": v(80.95, -46.47) * mm, "end": v(80.95, -42.47) * mm});
            skPoint(sketch, "E433.MirrorP", {"position": v(83.95, -46.47) * mm});
            skLineSegment(sketch, "E434.MirrorCS", {"start": v(83.95, -42.47) * mm, "end": v(80.95, -42.47) * mm});
            skLineSegment(sketch, "E435.MirrorCS", {"start": v(85.95, -43.97) * mm, "end": v(83.95, -43.97) * mm});
            skLineSegment(sketch, "E436.MirrorCS", {"start": v(83.95, -50.47) * mm, "end": v(80.95, -50.47) * mm});
            skPoint(sketch, "E437.MirrorP", {"position": v(83.95, -48.97) * mm});
            skLineSegment(sketch, "E438.MirrorCS", {"start": v(78.45, -54.47) * mm, "end": v(79.95, -54.47) * mm});
            skLineSegment(sketch, "E439.MirrorCS", {"start": v(78.45, -56.47) * mm, "end": v(78.45, -54.47) * mm});
            skLineSegment(sketch, "E440.MirrorCS", {"start": v(73.45, -56.47) * mm, "end": v(73.45, -54.47) * mm});
            skLineSegment(sketch, "E441.MirrorCS", {"start": v(73.45, -54.47) * mm, "end": v(71.95, -54.47) * mm});
            skLineSegment(sketch, "E442.MirrorCS", {"start": v(71.95, -54.47) * mm, "end": v(71.95, -51.47) * mm});
            skLineSegment(sketch, "E443.MirrorCS", {"start": v(75.95, -51.47) * mm, "end": v(71.95, -51.47) * mm});
            skLineSegment(sketch, "E444.MirrorCS", {"start": v(79.95, -54.47) * mm, "end": v(79.95, -51.47) * mm});
            skLineSegment(sketch, "E445.MirrorCS", {"start": v(75.95, -51.47) * mm, "end": v(79.95, -51.47) * mm});
            skLineSegment(sketch, "E446.trimOffspring", {"start": v(85.95, -48.97) * mm, "end": v(85.95, -56.47) * mm});
            skLineSegment(sketch, "E447.trimOffspring", {"start": v(78.45, -56.47) * mm, "end": v(85.95, -56.47) * mm});
            skLineSegment(sketch, "E448.trimOffspring", {"start": v(65.95, -48.97) * mm, "end": v(65.95, -56.47) * mm});
            skPoint(sketch, "E449.orphan", {"position": v(65.95, -56.47) * mm});
            skSolve(sketch);
        }
        {
            var Q0;
            Q0=makeQuery(id+"F2.imprint","IMPRINT",FACE,{"disambiguationData":[TD([[makeQuery(id+"F2.imprint","IMPRINT",EDGE,{"derivedFrom":sQuery(id+"F2.wireOp",EDGE,"E360.bottom")}),-1.0]])]});
            var Q1;
            Q1=makeQuery(id+"F2.imprint","IMPRINT",FACE,{"disambiguationData":[TD([[makeQuery(id+"F2.imprint","IMPRINT",EDGE,{"derivedFrom":sQuery(id+"F2.wireOp",EDGE,"E405.bottom")}),-1.0]])]});
            extrude(context, id + "F3", {"entities" : qUnion([Q0, Q1]), "depth" : 365 * mm});
        }
        {
            var Q0;
            Q0=qCreatedBy(makeId("Front.planeOp"),FACE);
            var sketch = newSketch(context, id + "F4", { "sketchPlane" : qUnion([Q0])});
            skLineSegment(sketch, "E450.bottom", {"start": v(88.67, 82.78) * mm, "end": v(96.17, 82.78) * mm});
            skLineSegment(sketch, "E450.top", {"start": v(88.67, 62.78) * mm, "end": v(96.17, 62.78) * mm});
            skLineSegment(sketch, "E450.left", {"start": v(88.67, 82.78) * mm, "end": v(88.67, 75.28) * mm});
            skLineSegment(sketch, "E450.right", {"start": v(108.67, 82.78) * mm, "end": v(108.67, 75.28) * mm});
            skLineSegment(sketch, "E451.right", {"start": v(101.17, 82.78) * mm, "end": v(101.17, 80.78) * mm});
            skCircle(sketch, "E452", {"center": v(98.67, 72.78) * mm, "radius": 2.5 * mm});
            skLineSegment(sketch, "E453.MirrorCS", {"start": v(96.17, 82.78) * mm, "end": v(96.17, 80.78) * mm});
            skLineSegment(sketch, "E454.bottom", {"start": v(101.17, 80.78) * mm, "end": v(102.67, 80.78) * mm});
            skLineSegment(sketch, "E454.top", {"start": v(98.67, 77.78) * mm, "end": v(102.67, 77.78) * mm});
            skLineSegment(sketch, "E454.right", {"start": v(102.67, 80.78) * mm, "end": v(102.67, 77.78) * mm});
            skLineSegment(sketch, "E455.MirrorCS", {"start": v(94.67, 80.78) * mm, "end": v(94.67, 77.78) * mm});
            skLineSegment(sketch, "E456.MirrorCS", {"start": v(96.17, 80.78) * mm, "end": v(94.67, 80.78) * mm});
            skLineSegment(sketch, "E457.MirrorCS", {"start": v(98.67, 77.78) * mm, "end": v(94.67, 77.78) * mm});
            skPoint(sketch, "E458.MirrorCS.end.orphan", {"position": v(96.17, 80.78) * mm});
            skPoint(sketch, "E458.MirrorCS.start.orphan", {"position": v(98.67, 80.78) * mm});
            skLineSegment(sketch, "E459.trimOffspring", {"start": v(101.17, 82.78) * mm, "end": v(108.67, 82.78) * mm});
            skPoint(sketch, "E451.bottom.start.orphan", {"position": v(98.67, 82.78) * mm});
            skLineSegment(sketch, "E460.MirrorCS", {"start": v(90.67, 75.28) * mm, "end": v(90.67, 76.78) * mm});
            skLineSegment(sketch, "E461.MirrorCS", {"start": v(93.67, 72.78) * mm, "end": v(93.67, 76.78) * mm});
            skLineSegment(sketch, "E462.MirrorCS", {"start": v(90.67, 68.78) * mm, "end": v(93.67, 68.78) * mm});
            skLineSegment(sketch, "E463.MirrorCS", {"start": v(93.67, 72.78) * mm, "end": v(93.67, 68.78) * mm});
            skLineSegment(sketch, "E464.MirrorCS", {"start": v(90.67, 70.28) * mm, "end": v(90.67, 68.78) * mm});
            skLineSegment(sketch, "E465.MirrorCS", {"start": v(90.67, 76.78) * mm, "end": v(93.67, 76.78) * mm});
            skPoint(sketch, "E466.MirrorP", {"position": v(90.67, 75.28) * mm});
            skPoint(sketch, "E467.MirrorP", {"position": v(88.67, 72.78) * mm});
            skLineSegment(sketch, "E468.MirrorCS", {"start": v(88.67, 75.28) * mm, "end": v(90.67, 75.28) * mm});
            skLineSegment(sketch, "E469.MirrorCS", {"start": v(88.67, 70.28) * mm, "end": v(90.67, 70.28) * mm});
            skPoint(sketch, "E470.MirrorP", {"position": v(90.67, 72.78) * mm});
            skPoint(sketch, "E471.orphan", {"position": v(108.67, 82.78) * mm});
            skPoint(sketch, "E472.MirrorP", {"position": v(108.67, 72.78) * mm});
            skLineSegment(sketch, "E473.MirrorCS", {"start": v(106.67, 70.28) * mm, "end": v(106.67, 68.78) * mm});
            skLineSegment(sketch, "E474.MirrorCS", {"start": v(103.67, 72.78) * mm, "end": v(103.67, 68.78) * mm});
            skLineSegment(sketch, "E475.MirrorCS", {"start": v(108.67, 70.28) * mm, "end": v(106.67, 70.28) * mm});
            skLineSegment(sketch, "E476.MirrorCS", {"start": v(106.67, 75.28) * mm, "end": v(106.67, 76.78) * mm});
            skLineSegment(sketch, "E477.MirrorCS", {"start": v(103.67, 72.78) * mm, "end": v(103.67, 76.78) * mm});
            skPoint(sketch, "E478.MirrorP", {"position": v(106.67, 72.78) * mm});
            skLineSegment(sketch, "E479.MirrorCS", {"start": v(106.67, 76.78) * mm, "end": v(103.67, 76.78) * mm});
            skLineSegment(sketch, "E480.MirrorCS", {"start": v(108.67, 75.28) * mm, "end": v(106.67, 75.28) * mm});
            skLineSegment(sketch, "E481.MirrorCS", {"start": v(106.67, 68.78) * mm, "end": v(103.67, 68.78) * mm});
            skPoint(sketch, "E482.MirrorP", {"position": v(106.67, 70.28) * mm});
            skLineSegment(sketch, "E483.MirrorCS", {"start": v(101.17, 64.78) * mm, "end": v(102.67, 64.78) * mm});
            skLineSegment(sketch, "E484.MirrorCS", {"start": v(101.17, 62.78) * mm, "end": v(101.17, 64.78) * mm});
            skLineSegment(sketch, "E485.MirrorCS", {"start": v(96.17, 62.78) * mm, "end": v(96.17, 64.78) * mm});
            skLineSegment(sketch, "E486.MirrorCS", {"start": v(96.17, 64.78) * mm, "end": v(94.67, 64.78) * mm});
            skLineSegment(sketch, "E487.MirrorCS", {"start": v(94.67, 64.78) * mm, "end": v(94.67, 67.78) * mm});
            skLineSegment(sketch, "E488.MirrorCS", {"start": v(98.67, 67.78) * mm, "end": v(94.67, 67.78) * mm});
            skLineSegment(sketch, "E489.MirrorCS", {"start": v(102.67, 64.78) * mm, "end": v(102.67, 67.78) * mm});
            skLineSegment(sketch, "E490.MirrorCS", {"start": v(98.67, 67.78) * mm, "end": v(102.67, 67.78) * mm});
            skLineSegment(sketch, "E491.trimOffspring", {"start": v(108.67, 70.28) * mm, "end": v(108.67, 62.78) * mm});
            skLineSegment(sketch, "E492.trimOffspring", {"start": v(101.17, 62.78) * mm, "end": v(108.67, 62.78) * mm});
            skLineSegment(sketch, "E493.trimOffspring", {"start": v(88.67, 70.28) * mm, "end": v(88.67, 62.78) * mm});
            skPoint(sketch, "E494.orphan", {"position": v(88.67, 62.78) * mm});
            skLineSegment(sketch, "E495.bottom", {"start": v(140.12, 78.97) * mm, "end": v(147.62, 78.97) * mm});
            skLineSegment(sketch, "E495.top", {"start": v(140.12, 58.97) * mm, "end": v(147.62, 58.97) * mm});
            skLineSegment(sketch, "E495.left", {"start": v(140.12, 78.97) * mm, "end": v(140.12, 71.47) * mm});
            skLineSegment(sketch, "E495.right", {"start": v(160.12, 78.97) * mm, "end": v(160.12, 71.47) * mm});
            skLineSegment(sketch, "E496.right", {"start": v(152.62, 78.97) * mm, "end": v(152.62, 76.97) * mm});
            skCircle(sketch, "E497", {"center": v(150.12, 68.97) * mm, "radius": 2.5 * mm});
            skLineSegment(sketch, "E498.MirrorCS", {"start": v(147.62, 78.97) * mm, "end": v(147.62, 76.97) * mm});
            skLineSegment(sketch, "E499.bottom", {"start": v(152.62, 76.97) * mm, "end": v(154.12, 76.97) * mm});
            skLineSegment(sketch, "E499.top", {"start": v(150.12, 73.97) * mm, "end": v(154.12, 73.97) * mm});
            skLineSegment(sketch, "E499.right", {"start": v(154.12, 76.97) * mm, "end": v(154.12, 73.97) * mm});
            skLineSegment(sketch, "E500.MirrorCS", {"start": v(146.12, 76.97) * mm, "end": v(146.12, 73.97) * mm});
            skLineSegment(sketch, "E501.MirrorCS", {"start": v(147.62, 76.97) * mm, "end": v(146.12, 76.97) * mm});
            skLineSegment(sketch, "E502.MirrorCS", {"start": v(150.12, 73.97) * mm, "end": v(146.12, 73.97) * mm});
            skPoint(sketch, "E503.MirrorCS.end.orphan", {"position": v(147.62, 76.97) * mm});
            skPoint(sketch, "E503.MirrorCS.start.orphan", {"position": v(150.12, 76.97) * mm});
            skLineSegment(sketch, "E504.trimOffspring", {"start": v(152.62, 78.97) * mm, "end": v(160.12, 78.97) * mm});
            skPoint(sketch, "E496.bottom.start.orphan", {"position": v(150.12, 78.97) * mm});
            skLineSegment(sketch, "E505.MirrorCS", {"start": v(142.12, 71.47) * mm, "end": v(142.12, 72.97) * mm});
            skLineSegment(sketch, "E506.MirrorCS", {"start": v(145.12, 68.97) * mm, "end": v(145.12, 72.97) * mm});
            skLineSegment(sketch, "E507.MirrorCS", {"start": v(142.12, 64.97) * mm, "end": v(145.12, 64.97) * mm});
            skLineSegment(sketch, "E508.MirrorCS", {"start": v(145.12, 68.97) * mm, "end": v(145.12, 64.97) * mm});
            skLineSegment(sketch, "E509.MirrorCS", {"start": v(142.12, 66.47) * mm, "end": v(142.12, 64.97) * mm});
            skLineSegment(sketch, "E510.MirrorCS", {"start": v(142.12, 72.97) * mm, "end": v(145.12, 72.97) * mm});
            skPoint(sketch, "E511.MirrorP", {"position": v(142.12, 71.47) * mm});
            skPoint(sketch, "E512.MirrorP", {"position": v(140.12, 68.97) * mm});
            skLineSegment(sketch, "E513.MirrorCS", {"start": v(140.12, 71.47) * mm, "end": v(142.12, 71.47) * mm});
            skLineSegment(sketch, "E514.MirrorCS", {"start": v(140.12, 66.47) * mm, "end": v(142.12, 66.47) * mm});
            skPoint(sketch, "E515.MirrorP", {"position": v(142.12, 68.97) * mm});
            skPoint(sketch, "E516.orphan", {"position": v(160.12, 78.97) * mm});
            skPoint(sketch, "E517.MirrorP", {"position": v(160.12, 68.97) * mm});
            skLineSegment(sketch, "E518.MirrorCS", {"start": v(158.12, 66.47) * mm, "end": v(158.12, 64.97) * mm});
            skLineSegment(sketch, "E519.MirrorCS", {"start": v(155.12, 68.97) * mm, "end": v(155.12, 64.97) * mm});
            skLineSegment(sketch, "E520.MirrorCS", {"start": v(160.12, 66.47) * mm, "end": v(158.12, 66.47) * mm});
            skLineSegment(sketch, "E521.MirrorCS", {"start": v(158.12, 71.47) * mm, "end": v(158.12, 72.97) * mm});
            skLineSegment(sketch, "E522.MirrorCS", {"start": v(155.12, 68.97) * mm, "end": v(155.12, 72.97) * mm});
            skPoint(sketch, "E523.MirrorP", {"position": v(158.12, 68.97) * mm});
            skLineSegment(sketch, "E524.MirrorCS", {"start": v(158.12, 72.97) * mm, "end": v(155.12, 72.97) * mm});
            skLineSegment(sketch, "E525.MirrorCS", {"start": v(160.12, 71.47) * mm, "end": v(158.12, 71.47) * mm});
            skLineSegment(sketch, "E526.MirrorCS", {"start": v(158.12, 64.97) * mm, "end": v(155.12, 64.97) * mm});
            skPoint(sketch, "E527.MirrorP", {"position": v(158.12, 66.47) * mm});
            skLineSegment(sketch, "E528.MirrorCS", {"start": v(152.62, 60.97) * mm, "end": v(154.12, 60.97) * mm});
            skLineSegment(sketch, "E529.MirrorCS", {"start": v(152.62, 58.97) * mm, "end": v(152.62, 60.97) * mm});
            skLineSegment(sketch, "E530.MirrorCS", {"start": v(147.62, 58.97) * mm, "end": v(147.62, 60.97) * mm});
            skLineSegment(sketch, "E531.MirrorCS", {"start": v(147.62, 60.97) * mm, "end": v(146.12, 60.97) * mm});
            skLineSegment(sketch, "E532.MirrorCS", {"start": v(146.12, 60.97) * mm, "end": v(146.12, 63.97) * mm});
            skLineSegment(sketch, "E533.MirrorCS", {"start": v(150.12, 63.97) * mm, "end": v(146.12, 63.97) * mm});
            skLineSegment(sketch, "E534.MirrorCS", {"start": v(154.12, 60.97) * mm, "end": v(154.12, 63.97) * mm});
            skLineSegment(sketch, "E535.MirrorCS", {"start": v(150.12, 63.97) * mm, "end": v(154.12, 63.97) * mm});
            skLineSegment(sketch, "E536.trimOffspring", {"start": v(160.12, 66.47) * mm, "end": v(160.12, 58.97) * mm});
            skLineSegment(sketch, "E537.trimOffspring", {"start": v(152.62, 58.97) * mm, "end": v(160.12, 58.97) * mm});
            skLineSegment(sketch, "E538.trimOffspring", {"start": v(140.12, 66.47) * mm, "end": v(140.12, 58.97) * mm});
            skPoint(sketch, "E539.orphan", {"position": v(140.12, 58.97) * mm});
            skSolve(sketch);
        }
        {
            var Q0;
            Q0=makeQuery(id+"F4.imprint","IMPRINT",FACE,{"disambiguationData":[TD([[makeQuery(id+"F4.imprint","IMPRINT",EDGE,{"derivedFrom":sQuery(id+"F4.wireOp",EDGE,"E450.bottom")}),-1.0]])]});
            var Q1;
            Q1=makeQuery(id+"F4.imprint","IMPRINT",FACE,{"disambiguationData":[TD([[makeQuery(id+"F4.imprint","IMPRINT",EDGE,{"derivedFrom":sQuery(id+"F4.wireOp",EDGE,"E495.bottom")}),-1.0]])]});
            extrude(context, id + "F5", {"entities" : qUnion([Q0, Q1]), "depth" : 120 * mm});
        }
        {
            var Q0;
            Q0=qCreatedBy(makeId("Front.planeOp"),FACE);
            var sketch = newSketch(context, id + "F6", { "sketchPlane" : qUnion([Q0])});
            skLineSegment(sketch, "E540.bottom", {"start": v(160.13, -12.75) * mm, "end": v(167.63, -12.75) * mm});
            skLineSegment(sketch, "E540.top", {"start": v(160.13, -32.75) * mm, "end": v(167.63, -32.75) * mm});
            skLineSegment(sketch, "E540.left", {"start": v(160.13, -12.75) * mm, "end": v(160.13, -20.25) * mm});
            skLineSegment(sketch, "E540.right", {"start": v(180.13, -12.75) * mm, "end": v(180.13, -20.25) * mm});
            skLineSegment(sketch, "E541.right", {"start": v(172.63, -12.75) * mm, "end": v(172.63, -14.75) * mm});
            skCircle(sketch, "E542", {"center": v(170.13, -22.75) * mm, "radius": 2.5 * mm});
            skLineSegment(sketch, "E543.MirrorCS", {"start": v(167.63, -12.75) * mm, "end": v(167.63, -14.75) * mm});
            skLineSegment(sketch, "E544.bottom", {"start": v(172.63, -14.75) * mm, "end": v(174.13, -14.75) * mm});
            skLineSegment(sketch, "E544.top", {"start": v(170.13, -17.75) * mm, "end": v(174.13, -17.75) * mm});
            skLineSegment(sketch, "E544.right", {"start": v(174.13, -14.75) * mm, "end": v(174.13, -17.75) * mm});
            skLineSegment(sketch, "E545.MirrorCS", {"start": v(166.13, -14.75) * mm, "end": v(166.13, -17.75) * mm});
            skLineSegment(sketch, "E546.MirrorCS", {"start": v(167.63, -14.75) * mm, "end": v(166.13, -14.75) * mm});
            skLineSegment(sketch, "E547.MirrorCS", {"start": v(170.13, -17.75) * mm, "end": v(166.13, -17.75) * mm});
            skPoint(sketch, "E548.MirrorCS.end.orphan", {"position": v(167.63, -14.75) * mm});
            skPoint(sketch, "E548.MirrorCS.start.orphan", {"position": v(170.13, -14.75) * mm});
            skLineSegment(sketch, "E549.trimOffspring", {"start": v(172.63, -12.75) * mm, "end": v(180.13, -12.75) * mm});
            skPoint(sketch, "E541.bottom.start.orphan", {"position": v(170.13, -12.75) * mm});
            skLineSegment(sketch, "E550.MirrorCS", {"start": v(162.13, -20.25) * mm, "end": v(162.13, -18.75) * mm});
            skLineSegment(sketch, "E551.MirrorCS", {"start": v(165.13, -22.75) * mm, "end": v(165.13, -18.75) * mm});
            skLineSegment(sketch, "E552.MirrorCS", {"start": v(162.13, -26.75) * mm, "end": v(165.13, -26.75) * mm});
            skLineSegment(sketch, "E553.MirrorCS", {"start": v(165.13, -22.75) * mm, "end": v(165.13, -26.75) * mm});
            skLineSegment(sketch, "E554.MirrorCS", {"start": v(162.13, -25.25) * mm, "end": v(162.13, -26.75) * mm});
            skLineSegment(sketch, "E555.MirrorCS", {"start": v(162.13, -18.75) * mm, "end": v(165.13, -18.75) * mm});
            skPoint(sketch, "E556.MirrorP", {"position": v(162.13, -20.25) * mm});
            skPoint(sketch, "E557.MirrorP", {"position": v(160.13, -22.75) * mm});
            skLineSegment(sketch, "E558.MirrorCS", {"start": v(160.13, -20.25) * mm, "end": v(162.13, -20.25) * mm});
            skLineSegment(sketch, "E559.MirrorCS", {"start": v(160.13, -25.25) * mm, "end": v(162.13, -25.25) * mm});
            skPoint(sketch, "E560.MirrorP", {"position": v(162.13, -22.75) * mm});
            skPoint(sketch, "E561.orphan", {"position": v(180.13, -12.75) * mm});
            skPoint(sketch, "E562.MirrorP", {"position": v(180.13, -22.75) * mm});
            skLineSegment(sketch, "E563.MirrorCS", {"start": v(178.13, -25.25) * mm, "end": v(178.13, -26.75) * mm});
            skLineSegment(sketch, "E564.MirrorCS", {"start": v(175.13, -22.75) * mm, "end": v(175.13, -26.75) * mm});
            skLineSegment(sketch, "E565.MirrorCS", {"start": v(180.13, -25.25) * mm, "end": v(178.13, -25.25) * mm});
            skLineSegment(sketch, "E566.MirrorCS", {"start": v(178.13, -20.25) * mm, "end": v(178.13, -18.75) * mm});
            skLineSegment(sketch, "E567.MirrorCS", {"start": v(175.13, -22.75) * mm, "end": v(175.13, -18.75) * mm});
            skPoint(sketch, "E568.MirrorP", {"position": v(178.13, -22.75) * mm});
            skLineSegment(sketch, "E569.MirrorCS", {"start": v(178.13, -18.75) * mm, "end": v(175.13, -18.75) * mm});
            skLineSegment(sketch, "E570.MirrorCS", {"start": v(180.13, -20.25) * mm, "end": v(178.13, -20.25) * mm});
            skLineSegment(sketch, "E571.MirrorCS", {"start": v(178.13, -26.75) * mm, "end": v(175.13, -26.75) * mm});
            skPoint(sketch, "E572.MirrorP", {"position": v(178.13, -25.25) * mm});
            skLineSegment(sketch, "E573.MirrorCS", {"start": v(172.63, -30.75) * mm, "end": v(174.13, -30.75) * mm});
            skLineSegment(sketch, "E574.MirrorCS", {"start": v(172.63, -32.75) * mm, "end": v(172.63, -30.75) * mm});
            skLineSegment(sketch, "E575.MirrorCS", {"start": v(167.63, -32.75) * mm, "end": v(167.63, -30.75) * mm});
            skLineSegment(sketch, "E576.MirrorCS", {"start": v(167.63, -30.75) * mm, "end": v(166.13, -30.75) * mm});
            skLineSegment(sketch, "E577.MirrorCS", {"start": v(166.13, -30.75) * mm, "end": v(166.13, -27.75) * mm});
            skLineSegment(sketch, "E578.MirrorCS", {"start": v(170.13, -27.75) * mm, "end": v(166.13, -27.75) * mm});
            skLineSegment(sketch, "E579.MirrorCS", {"start": v(174.13, -30.75) * mm, "end": v(174.13, -27.75) * mm});
            skLineSegment(sketch, "E580.MirrorCS", {"start": v(170.13, -27.75) * mm, "end": v(174.13, -27.75) * mm});
            skLineSegment(sketch, "E581.trimOffspring", {"start": v(180.13, -25.25) * mm, "end": v(180.13, -32.75) * mm});
            skLineSegment(sketch, "E582.trimOffspring", {"start": v(172.63, -32.75) * mm, "end": v(180.13, -32.75) * mm});
            skLineSegment(sketch, "E583.trimOffspring", {"start": v(160.13, -25.25) * mm, "end": v(160.13, -32.75) * mm});
            skPoint(sketch, "E584.orphan", {"position": v(160.13, -32.75) * mm});
            skSolve(sketch);
        }
        {
            var Q0;
            Q0=makeQuery(id+"F6.imprint","IMPRINT",FACE,{"disambiguationData":[TD([[makeQuery(id+"F6.imprint","IMPRINT",EDGE,{"derivedFrom":sQuery(id+"F6.wireOp",EDGE,"E540.bottom")}),-1.0]])]});
            extrude(context, id + "F7", {"entities" : qUnion([Q0]), "depth" : 375 * mm});
        }
        {
            var Q0;
            Q0=qCreatedBy(makeId("Front.planeOp"),FACE);
            var sketch = newSketch(context, id + "F8", { "sketchPlane" : qUnion([Q0])});
            skLineSegment(sketch, "E585.bottom", {"start": v(-110.92, -28.96) * mm, "end": v(-103.42, -28.96) * mm});
            skLineSegment(sketch, "E585.top", {"start": v(-110.92, -48.96) * mm, "end": v(-103.42, -48.96) * mm});
            skLineSegment(sketch, "E585.left", {"start": v(-110.92, -28.96) * mm, "end": v(-110.92, -36.46) * mm});
            skLineSegment(sketch, "E585.right", {"start": v(-90.92, -28.96) * mm, "end": v(-90.92, -36.46) * mm});
            skLineSegment(sketch, "E586.right", {"start": v(-98.42, -28.96) * mm, "end": v(-98.42, -30.96) * mm});
            skCircle(sketch, "E587", {"center": v(-100.92, -38.96) * mm, "radius": 2.5 * mm});
            skLineSegment(sketch, "E588.MirrorCS", {"start": v(-103.42, -28.96) * mm, "end": v(-103.42, -30.96) * mm});
            skLineSegment(sketch, "E589.bottom", {"start": v(-98.42, -30.96) * mm, "end": v(-96.92, -30.96) * mm});
            skLineSegment(sketch, "E589.top", {"start": v(-100.92, -33.96) * mm, "end": v(-96.92, -33.96) * mm});
            skLineSegment(sketch, "E589.right", {"start": v(-96.92, -30.96) * mm, "end": v(-96.92, -33.96) * mm});
            skLineSegment(sketch, "E590.MirrorCS", {"start": v(-104.92, -30.96) * mm, "end": v(-104.92, -33.96) * mm});
            skLineSegment(sketch, "E591.MirrorCS", {"start": v(-103.42, -30.96) * mm, "end": v(-104.92, -30.96) * mm});
            skLineSegment(sketch, "E592.MirrorCS", {"start": v(-100.92, -33.96) * mm, "end": v(-104.92, -33.96) * mm});
            skPoint(sketch, "E593.MirrorCS.end.orphan", {"position": v(-103.42, -30.96) * mm});
            skPoint(sketch, "E593.MirrorCS.start.orphan", {"position": v(-100.92, -30.96) * mm});
            skLineSegment(sketch, "E594.trimOffspring", {"start": v(-98.42, -28.96) * mm, "end": v(-90.92, -28.96) * mm});
            skPoint(sketch, "E586.bottom.start.orphan", {"position": v(-100.92, -28.96) * mm});
            skLineSegment(sketch, "E595.MirrorCS", {"start": v(-108.92, -36.46) * mm, "end": v(-108.92, -34.96) * mm});
            skLineSegment(sketch, "E596.MirrorCS", {"start": v(-105.92, -38.96) * mm, "end": v(-105.92, -34.96) * mm});
            skLineSegment(sketch, "E597.MirrorCS", {"start": v(-108.92, -42.96) * mm, "end": v(-105.92, -42.96) * mm});
            skLineSegment(sketch, "E598.MirrorCS", {"start": v(-105.92, -38.96) * mm, "end": v(-105.92, -42.96) * mm});
            skLineSegment(sketch, "E599.MirrorCS", {"start": v(-108.92, -41.46) * mm, "end": v(-108.92, -42.96) * mm});
            skLineSegment(sketch, "E600.MirrorCS", {"start": v(-108.92, -34.96) * mm, "end": v(-105.92, -34.96) * mm});
            skPoint(sketch, "E601.MirrorP", {"position": v(-108.92, -36.46) * mm});
            skPoint(sketch, "E602.MirrorP", {"position": v(-110.92, -38.96) * mm});
            skLineSegment(sketch, "E603.MirrorCS", {"start": v(-110.92, -36.46) * mm, "end": v(-108.92, -36.46) * mm});
            skLineSegment(sketch, "E604.MirrorCS", {"start": v(-110.92, -41.46) * mm, "end": v(-108.92, -41.46) * mm});
            skPoint(sketch, "E605.MirrorP", {"position": v(-108.92, -38.96) * mm});
            skPoint(sketch, "E606.orphan", {"position": v(-90.92, -28.96) * mm});
            skPoint(sketch, "E607.MirrorP", {"position": v(-90.92, -38.96) * mm});
            skLineSegment(sketch, "E608.MirrorCS", {"start": v(-92.92, -41.46) * mm, "end": v(-92.92, -42.96) * mm});
            skLineSegment(sketch, "E609.MirrorCS", {"start": v(-95.92, -38.96) * mm, "end": v(-95.92, -42.96) * mm});
            skLineSegment(sketch, "E610.MirrorCS", {"start": v(-90.92, -41.46) * mm, "end": v(-92.92, -41.46) * mm});
            skLineSegment(sketch, "E611.MirrorCS", {"start": v(-92.92, -36.46) * mm, "end": v(-92.92, -34.96) * mm});
            skLineSegment(sketch, "E612.MirrorCS", {"start": v(-95.92, -38.96) * mm, "end": v(-95.92, -34.96) * mm});
            skPoint(sketch, "E613.MirrorP", {"position": v(-92.92, -38.96) * mm});
            skLineSegment(sketch, "E614.MirrorCS", {"start": v(-92.92, -34.96) * mm, "end": v(-95.92, -34.96) * mm});
            skLineSegment(sketch, "E615.MirrorCS", {"start": v(-90.92, -36.46) * mm, "end": v(-92.92, -36.46) * mm});
            skLineSegment(sketch, "E616.MirrorCS", {"start": v(-92.92, -42.96) * mm, "end": v(-95.92, -42.96) * mm});
            skPoint(sketch, "E617.MirrorP", {"position": v(-92.92, -41.46) * mm});
            skLineSegment(sketch, "E618.MirrorCS", {"start": v(-98.42, -46.96) * mm, "end": v(-96.92, -46.96) * mm});
            skLineSegment(sketch, "E619.MirrorCS", {"start": v(-98.42, -48.96) * mm, "end": v(-98.42, -46.96) * mm});
            skLineSegment(sketch, "E620.MirrorCS", {"start": v(-103.42, -48.96) * mm, "end": v(-103.42, -46.96) * mm});
            skLineSegment(sketch, "E621.MirrorCS", {"start": v(-103.42, -46.96) * mm, "end": v(-104.92, -46.96) * mm});
            skLineSegment(sketch, "E622.MirrorCS", {"start": v(-104.92, -46.96) * mm, "end": v(-104.92, -43.96) * mm});
            skLineSegment(sketch, "E623.MirrorCS", {"start": v(-100.92, -43.96) * mm, "end": v(-104.92, -43.96) * mm});
            skLineSegment(sketch, "E624.MirrorCS", {"start": v(-96.92, -46.96) * mm, "end": v(-96.92, -43.96) * mm});
            skLineSegment(sketch, "E625.MirrorCS", {"start": v(-100.92, -43.96) * mm, "end": v(-96.92, -43.96) * mm});
            skLineSegment(sketch, "E626.trimOffspring", {"start": v(-90.92, -41.46) * mm, "end": v(-90.92, -48.96) * mm});
            skLineSegment(sketch, "E627.trimOffspring", {"start": v(-98.42, -48.96) * mm, "end": v(-90.92, -48.96) * mm});
            skLineSegment(sketch, "E628.trimOffspring", {"start": v(-110.92, -41.46) * mm, "end": v(-110.92, -48.96) * mm});
            skPoint(sketch, "E629.orphan", {"position": v(-110.92, -48.96) * mm});
            skLineSegment(sketch, "E630.bottom", {"start": v(-60.91, -34.56) * mm, "end": v(-53.41, -34.56) * mm});
            skLineSegment(sketch, "E630.top", {"start": v(-60.91, -54.56) * mm, "end": v(-53.41, -54.56) * mm});
            skLineSegment(sketch, "E630.left", {"start": v(-60.91, -34.56) * mm, "end": v(-60.91, -42.06) * mm});
            skLineSegment(sketch, "E630.right", {"start": v(-40.91, -34.56) * mm, "end": v(-40.91, -42.06) * mm});
            skLineSegment(sketch, "E631.right", {"start": v(-48.41, -34.56) * mm, "end": v(-48.41, -36.56) * mm});
            skCircle(sketch, "E632", {"center": v(-50.91, -44.56) * mm, "radius": 2.5 * mm});
            skLineSegment(sketch, "E633.MirrorCS", {"start": v(-53.41, -34.56) * mm, "end": v(-53.41, -36.56) * mm});
            skLineSegment(sketch, "E634.bottom", {"start": v(-48.41, -36.56) * mm, "end": v(-46.91, -36.56) * mm});
            skLineSegment(sketch, "E634.top", {"start": v(-50.91, -39.56) * mm, "end": v(-46.91, -39.56) * mm});
            skLineSegment(sketch, "E634.right", {"start": v(-46.91, -36.56) * mm, "end": v(-46.91, -39.56) * mm});
            skLineSegment(sketch, "E635.MirrorCS", {"start": v(-54.91, -36.56) * mm, "end": v(-54.91, -39.56) * mm});
            skLineSegment(sketch, "E636.MirrorCS", {"start": v(-53.41, -36.56) * mm, "end": v(-54.91, -36.56) * mm});
            skLineSegment(sketch, "E637.MirrorCS", {"start": v(-50.91, -39.56) * mm, "end": v(-54.91, -39.56) * mm});
            skPoint(sketch, "E638.MirrorCS.end.orphan", {"position": v(-53.41, -36.56) * mm});
            skPoint(sketch, "E638.MirrorCS.start.orphan", {"position": v(-50.91, -36.56) * mm});
            skLineSegment(sketch, "E639.trimOffspring", {"start": v(-48.41, -34.56) * mm, "end": v(-40.91, -34.56) * mm});
            skPoint(sketch, "E631.bottom.start.orphan", {"position": v(-50.91, -34.56) * mm});
            skLineSegment(sketch, "E640.MirrorCS", {"start": v(-58.91, -42.06) * mm, "end": v(-58.91, -40.56) * mm});
            skLineSegment(sketch, "E641.MirrorCS", {"start": v(-55.91, -44.56) * mm, "end": v(-55.91, -40.56) * mm});
            skLineSegment(sketch, "E642.MirrorCS", {"start": v(-58.91, -48.56) * mm, "end": v(-55.91, -48.56) * mm});
            skLineSegment(sketch, "E643.MirrorCS", {"start": v(-55.91, -44.56) * mm, "end": v(-55.91, -48.56) * mm});
            skLineSegment(sketch, "E644.MirrorCS", {"start": v(-58.91, -47.06) * mm, "end": v(-58.91, -48.56) * mm});
            skLineSegment(sketch, "E645.MirrorCS", {"start": v(-58.91, -40.56) * mm, "end": v(-55.91, -40.56) * mm});
            skPoint(sketch, "E646.MirrorP", {"position": v(-58.91, -42.06) * mm});
            skPoint(sketch, "E647.MirrorP", {"position": v(-60.91, -44.56) * mm});
            skLineSegment(sketch, "E648.MirrorCS", {"start": v(-60.91, -42.06) * mm, "end": v(-58.91, -42.06) * mm});
            skLineSegment(sketch, "E649.MirrorCS", {"start": v(-60.91, -47.06) * mm, "end": v(-58.91, -47.06) * mm});
            skPoint(sketch, "E650.MirrorP", {"position": v(-58.91, -44.56) * mm});
            skPoint(sketch, "E651.orphan", {"position": v(-40.91, -34.56) * mm});
            skPoint(sketch, "E652.MirrorP", {"position": v(-40.91, -44.56) * mm});
            skLineSegment(sketch, "E653.MirrorCS", {"start": v(-42.91, -47.06) * mm, "end": v(-42.91, -48.56) * mm});
            skLineSegment(sketch, "E654.MirrorCS", {"start": v(-45.91, -44.56) * mm, "end": v(-45.91, -48.56) * mm});
            skLineSegment(sketch, "E655.MirrorCS", {"start": v(-40.91, -47.06) * mm, "end": v(-42.91, -47.06) * mm});
            skLineSegment(sketch, "E656.MirrorCS", {"start": v(-42.91, -42.06) * mm, "end": v(-42.91, -40.56) * mm});
            skLineSegment(sketch, "E657.MirrorCS", {"start": v(-45.91, -44.56) * mm, "end": v(-45.91, -40.56) * mm});
            skPoint(sketch, "E658.MirrorP", {"position": v(-42.91, -44.56) * mm});
            skLineSegment(sketch, "E659.MirrorCS", {"start": v(-42.91, -40.56) * mm, "end": v(-45.91, -40.56) * mm});
            skLineSegment(sketch, "E660.MirrorCS", {"start": v(-40.91, -42.06) * mm, "end": v(-42.91, -42.06) * mm});
            skLineSegment(sketch, "E661.MirrorCS", {"start": v(-42.91, -48.56) * mm, "end": v(-45.91, -48.56) * mm});
            skPoint(sketch, "E662.MirrorP", {"position": v(-42.91, -47.06) * mm});
            skLineSegment(sketch, "E663.MirrorCS", {"start": v(-48.41, -52.56) * mm, "end": v(-46.91, -52.56) * mm});
            skLineSegment(sketch, "E664.MirrorCS", {"start": v(-48.41, -54.56) * mm, "end": v(-48.41, -52.56) * mm});
            skLineSegment(sketch, "E665.MirrorCS", {"start": v(-53.41, -54.56) * mm, "end": v(-53.41, -52.56) * mm});
            skLineSegment(sketch, "E666.MirrorCS", {"start": v(-53.41, -52.56) * mm, "end": v(-54.91, -52.56) * mm});
            skLineSegment(sketch, "E667.MirrorCS", {"start": v(-54.91, -52.56) * mm, "end": v(-54.91, -49.56) * mm});
            skLineSegment(sketch, "E668.MirrorCS", {"start": v(-50.91, -49.56) * mm, "end": v(-54.91, -49.56) * mm});
            skLineSegment(sketch, "E669.MirrorCS", {"start": v(-46.91, -52.56) * mm, "end": v(-46.91, -49.56) * mm});
            skLineSegment(sketch, "E670.MirrorCS", {"start": v(-50.91, -49.56) * mm, "end": v(-46.91, -49.56) * mm});
            skLineSegment(sketch, "E671.trimOffspring", {"start": v(-40.91, -47.06) * mm, "end": v(-40.91, -54.56) * mm});
            skLineSegment(sketch, "E672.trimOffspring", {"start": v(-48.41, -54.56) * mm, "end": v(-40.91, -54.56) * mm});
            skLineSegment(sketch, "E673.trimOffspring", {"start": v(-60.91, -47.06) * mm, "end": v(-60.91, -54.56) * mm});
            skPoint(sketch, "E674.orphan", {"position": v(-60.91, -54.56) * mm});
            skSolve(sketch);
        }
        {
            var Q0;
            Q0=makeQuery(id+"F8.imprint","IMPRINT",FACE,{"disambiguationData":[TD([[makeQuery(id+"F8.imprint","IMPRINT",EDGE,{"derivedFrom":sQuery(id+"F8.wireOp",EDGE,"E585.bottom")}),-1.0]])]});
            var Q1;
            Q1=makeQuery(id+"F8.imprint","IMPRINT",FACE,{"disambiguationData":[TD([[makeQuery(id+"F8.imprint","IMPRINT",EDGE,{"derivedFrom":sQuery(id+"F8.wireOp",EDGE,"E630.bottom")}),-1.0]])]});
            extrude(context, id + "F9", {"entities" : qUnion([Q0, Q1]), "depth" : 500 * mm});
        }
        {
            var Q0;
            Q0=qCreatedBy(makeId("Front.planeOp"),FACE);
            var sketch = newSketch(context, id + "F10", { "sketchPlane" : qUnion([Q0])});
            skLineSegment(sketch, "E675.bottom", {"start": v(11.48, 23.2) * mm, "end": v(18.98, 23.2) * mm});
            skLineSegment(sketch, "E675.top", {"start": v(11.48, 3.2) * mm, "end": v(18.98, 3.2) * mm});
            skLineSegment(sketch, "E675.left", {"start": v(11.48, 23.2) * mm, "end": v(11.48, 15.7) * mm});
            skLineSegment(sketch, "E676.right", {"start": v(23.98, 23.2) * mm, "end": v(23.98, 21.2) * mm});
            skCircle(sketch, "E677", {"center": v(21.48, 13.2) * mm, "radius": 2.5 * mm});
            skLineSegment(sketch, "E678.MirrorCS", {"start": v(18.98, 23.2) * mm, "end": v(18.98, 21.2) * mm});
            skLineSegment(sketch, "E679.bottom", {"start": v(23.98, 21.2) * mm, "end": v(25.48, 21.2) * mm});
            skLineSegment(sketch, "E679.top", {"start": v(21.48, 18.2) * mm, "end": v(25.48, 18.2) * mm});
            skLineSegment(sketch, "E679.right", {"start": v(25.48, 21.2) * mm, "end": v(25.48, 18.2) * mm});
            skLineSegment(sketch, "E680.MirrorCS", {"start": v(17.48, 21.2) * mm, "end": v(17.48, 18.2) * mm});
            skLineSegment(sketch, "E681.MirrorCS", {"start": v(18.98, 21.2) * mm, "end": v(17.48, 21.2) * mm});
            skLineSegment(sketch, "E682.MirrorCS", {"start": v(21.48, 18.2) * mm, "end": v(17.48, 18.2) * mm});
            skPoint(sketch, "E683.MirrorCS.end.orphan", {"position": v(18.98, 21.2) * mm});
            skPoint(sketch, "E683.MirrorCS.start.orphan", {"position": v(21.48, 21.2) * mm});
            skLineSegment(sketch, "E684.trimOffspring", {"start": v(23.98, 23.2) * mm, "end": v(31.48, 23.2) * mm});
            skPoint(sketch, "E676.bottom.start.orphan", {"position": v(21.48, 23.2) * mm});
            skLineSegment(sketch, "E685.MirrorCS", {"start": v(13.48, 15.7) * mm, "end": v(13.48, 17.2) * mm});
            skLineSegment(sketch, "E686.MirrorCS", {"start": v(16.48, 13.2) * mm, "end": v(16.48, 17.2) * mm});
            skLineSegment(sketch, "E687.MirrorCS", {"start": v(13.48, 9.2) * mm, "end": v(16.48, 9.2) * mm});
            skLineSegment(sketch, "E688.MirrorCS", {"start": v(16.48, 13.2) * mm, "end": v(16.48, 9.2) * mm});
            skLineSegment(sketch, "E689.MirrorCS", {"start": v(13.48, 10.7) * mm, "end": v(13.48, 9.2) * mm});
            skLineSegment(sketch, "E690.MirrorCS", {"start": v(13.48, 17.2) * mm, "end": v(16.48, 17.2) * mm});
            skPoint(sketch, "E691.MirrorP", {"position": v(13.48, 15.7) * mm});
            skPoint(sketch, "E692.MirrorP", {"position": v(11.48, 13.2) * mm});
            skLineSegment(sketch, "E693.MirrorCS", {"start": v(11.48, 15.7) * mm, "end": v(13.48, 15.7) * mm});
            skLineSegment(sketch, "E694.MirrorCS", {"start": v(11.48, 10.7) * mm, "end": v(13.48, 10.7) * mm});
            skPoint(sketch, "E695.MirrorP", {"position": v(13.48, 13.2) * mm});
            skPoint(sketch, "E696.orphan", {"position": v(31.48, 23.2) * mm});
            skPoint(sketch, "E697.MirrorP", {"position": v(31.48, 13.2) * mm});
            skLineSegment(sketch, "E698.MirrorCS", {"start": v(29.48, 10.7) * mm, "end": v(29.48, 9.2) * mm});
            skLineSegment(sketch, "E699.MirrorCS", {"start": v(26.48, 13.2) * mm, "end": v(26.48, 9.2) * mm});
            skLineSegment(sketch, "E700.MirrorCS", {"start": v(31.48, 10.7) * mm, "end": v(29.48, 10.7) * mm});
            skLineSegment(sketch, "E701.MirrorCS", {"start": v(29.48, 15.7) * mm, "end": v(29.48, 17.2) * mm});
            skLineSegment(sketch, "E702.MirrorCS", {"start": v(26.48, 13.2) * mm, "end": v(26.48, 17.2) * mm});
            skPoint(sketch, "E703.MirrorP", {"position": v(29.48, 13.2) * mm});
            skLineSegment(sketch, "E704.MirrorCS", {"start": v(29.48, 17.2) * mm, "end": v(26.48, 17.2) * mm});
            skLineSegment(sketch, "E705.MirrorCS", {"start": v(31.48, 15.7) * mm, "end": v(29.48, 15.7) * mm});
            skLineSegment(sketch, "E706.MirrorCS", {"start": v(29.48, 9.2) * mm, "end": v(26.48, 9.2) * mm});
            skPoint(sketch, "E707.MirrorP", {"position": v(29.48, 10.7) * mm});
            skLineSegment(sketch, "E708.MirrorCS", {"start": v(23.98, 5.2) * mm, "end": v(25.48, 5.2) * mm});
            skLineSegment(sketch, "E709.MirrorCS", {"start": v(23.98, 3.2) * mm, "end": v(23.98, 5.2) * mm});
            skLineSegment(sketch, "E710.MirrorCS", {"start": v(18.98, 3.2) * mm, "end": v(18.98, 5.2) * mm});
            skLineSegment(sketch, "E711.MirrorCS", {"start": v(18.98, 5.2) * mm, "end": v(17.48, 5.2) * mm});
            skLineSegment(sketch, "E712.MirrorCS", {"start": v(17.48, 5.2) * mm, "end": v(17.48, 8.2) * mm});
            skLineSegment(sketch, "E713.MirrorCS", {"start": v(21.48, 8.2) * mm, "end": v(17.48, 8.2) * mm});
            skLineSegment(sketch, "E714.MirrorCS", {"start": v(25.48, 5.2) * mm, "end": v(25.48, 8.2) * mm});
            skLineSegment(sketch, "E715.MirrorCS", {"start": v(21.48, 8.2) * mm, "end": v(25.48, 8.2) * mm});
            skLineSegment(sketch, "E716.trimOffspring", {"start": v(23.98, 3.2) * mm, "end": v(31.48, 3.2) * mm});
            skLineSegment(sketch, "E717.trimOffspring", {"start": v(11.48, 10.7) * mm, "end": v(11.48, 3.2) * mm});
            skPoint(sketch, "E718.orphan", {"position": v(11.48, 3.2) * mm});
            skLineSegment(sketch, "E719.MirrorCS", {"start": v(43.98, 21.2) * mm, "end": v(45.48, 21.2) * mm});
            skLineSegment(sketch, "E720.MirrorCS", {"start": v(38.98, 21.2) * mm, "end": v(37.48, 21.2) * mm});
            skLineSegment(sketch, "E721.MirrorCS", {"start": v(49.48, 10.7) * mm, "end": v(49.48, 9.2) * mm});
            skLineSegment(sketch, "E722.MirrorCS", {"start": v(49.48, 15.7) * mm, "end": v(49.48, 17.2) * mm});
            skLineSegment(sketch, "E723.MirrorCS", {"start": v(38.98, 5.2) * mm, "end": v(37.48, 5.2) * mm});
            skLineSegment(sketch, "E724.MirrorCS", {"start": v(33.48, 10.7) * mm, "end": v(33.48, 9.2) * mm});
            skLineSegment(sketch, "E725.MirrorCS", {"start": v(43.98, 5.2) * mm, "end": v(45.48, 5.2) * mm});
            skLineSegment(sketch, "E726.MirrorCS", {"start": v(33.48, 15.7) * mm, "end": v(33.48, 17.2) * mm});
            skLineSegment(sketch, "E727.MirrorCS", {"start": v(51.48, 10.7) * mm, "end": v(49.48, 10.7) * mm});
            skPoint(sketch, "E728.MirrorP", {"position": v(41.48, 23.2) * mm});
            skPoint(sketch, "E729.MirrorP", {"position": v(49.48, 13.2) * mm});
            skLineSegment(sketch, "E730.MirrorCS", {"start": v(46.48, 13.2) * mm, "end": v(46.48, 9.2) * mm});
            skLineSegment(sketch, "E731.MirrorCS", {"start": v(49.48, 9.2) * mm, "end": v(46.48, 9.2) * mm});
            skLineSegment(sketch, "E732.MirrorCS", {"start": v(45.48, 21.2) * mm, "end": v(45.48, 18.2) * mm});
            skLineSegment(sketch, "E733.MirrorCS", {"start": v(51.48, 15.7) * mm, "end": v(49.48, 15.7) * mm});
            skLineSegment(sketch, "E734.MirrorCS", {"start": v(41.48, 18.2) * mm, "end": v(37.48, 18.2) * mm});
            skLineSegment(sketch, "E735.MirrorCS", {"start": v(49.48, 17.2) * mm, "end": v(46.48, 17.2) * mm});
            skLineSegment(sketch, "E736.MirrorCS", {"start": v(38.98, 23.2) * mm, "end": v(38.98, 21.2) * mm});
            skLineSegment(sketch, "E737.MirrorCS", {"start": v(43.98, 23.2) * mm, "end": v(43.98, 21.2) * mm});
            skPoint(sketch, "E738.MirrorP", {"position": v(41.48, 21.2) * mm});
            skPoint(sketch, "E739.MirrorP", {"position": v(51.48, 13.2) * mm});
            skPoint(sketch, "E740.MirrorP", {"position": v(43.98, 21.2) * mm});
            skLineSegment(sketch, "E741.MirrorCS", {"start": v(41.48, 18.2) * mm, "end": v(45.48, 18.2) * mm});
            skLineSegment(sketch, "E742.MirrorCS", {"start": v(46.48, 13.2) * mm, "end": v(46.48, 17.2) * mm});
            skPoint(sketch, "E743.MirrorP", {"position": v(49.48, 15.7) * mm});
            skLineSegment(sketch, "E744.MirrorCS", {"start": v(37.48, 21.2) * mm, "end": v(37.48, 18.2) * mm});
            skPoint(sketch, "E745.MirrorP", {"position": v(33.48, 10.7) * mm});
            skLineSegment(sketch, "E746.MirrorCS", {"start": v(41.48, 8.2) * mm, "end": v(37.48, 8.2) * mm});
            skLineSegment(sketch, "E747.MirrorCS", {"start": v(33.48, 9.2) * mm, "end": v(36.48, 9.2) * mm});
            skPoint(sketch, "E748.MirrorP", {"position": v(33.48, 13.2) * mm});
            skLineSegment(sketch, "E749.MirrorCS", {"start": v(37.48, 5.2) * mm, "end": v(37.48, 8.2) * mm});
            skLineSegment(sketch, "E750.MirrorCS", {"start": v(33.48, 17.2) * mm, "end": v(36.48, 17.2) * mm});
            skPoint(sketch, "E751.MirrorP", {"position": v(51.48, 3.2) * mm});
            skLineSegment(sketch, "E752.MirrorCS", {"start": v(36.48, 13.2) * mm, "end": v(36.48, 17.2) * mm});
            skLineSegment(sketch, "E753.MirrorCS", {"start": v(51.48, 23.2) * mm, "end": v(43.98, 23.2) * mm});
            skLineSegment(sketch, "E754.MirrorCS", {"start": v(51.48, 3.2) * mm, "end": v(43.98, 3.2) * mm});
            skLineSegment(sketch, "E755.MirrorCS", {"start": v(43.98, 3.2) * mm, "end": v(43.98, 5.2) * mm});
            skCircle(sketch, "E756.MirrorC", {"center": v(41.48, 13.2) * mm, "radius": 2.5 * mm});
            skLineSegment(sketch, "E757.MirrorCS", {"start": v(45.48, 5.2) * mm, "end": v(45.48, 8.2) * mm});
            skLineSegment(sketch, "E758.MirrorCS", {"start": v(36.48, 13.2) * mm, "end": v(36.48, 9.2) * mm});
            skLineSegment(sketch, "E759.MirrorCS", {"start": v(38.98, 3.2) * mm, "end": v(38.98, 5.2) * mm});
            skLineSegment(sketch, "E760.MirrorCS", {"start": v(41.48, 8.2) * mm, "end": v(45.48, 8.2) * mm});
            skLineSegment(sketch, "E761.MirrorCS", {"start": v(38.98, 23.2) * mm, "end": v(31.48, 23.2) * mm});
            skLineSegment(sketch, "E762.MirrorCS", {"start": v(38.98, 3.2) * mm, "end": v(31.48, 3.2) * mm});
            skLineSegment(sketch, "E763.MirrorCS", {"start": v(31.48, 10.7) * mm, "end": v(33.48, 10.7) * mm});
            skLineSegment(sketch, "E764.MirrorCS", {"start": v(31.48, 15.7) * mm, "end": v(33.48, 15.7) * mm});
            skLineSegment(sketch, "E765", {"start": v(51.48, 13.2) * mm, "end": v(51.48, 10.7) * mm});
            skLineSegment(sketch, "E766.MirrorCS", {"start": v(51.48, 10.7) * mm, "end": v(53.48, 10.7) * mm});
            skLineSegment(sketch, "E767.MirrorCS", {"start": v(51.48, 15.7) * mm, "end": v(53.48, 15.7) * mm});
            skLineSegment(sketch, "E768.MirrorCS", {"start": v(51.48, 23.2) * mm, "end": v(58.98, 23.2) * mm});
            skLineSegment(sketch, "E769.MirrorCS", {"start": v(51.48, 3.2) * mm, "end": v(58.98, 3.2) * mm});
            skLineSegment(sketch, "E770.MirrorCS", {"start": v(58.98, 21.2) * mm, "end": v(57.48, 21.2) * mm});
            skLineSegment(sketch, "E771.MirrorCS", {"start": v(89.48, 10.7) * mm, "end": v(89.48, 9.2) * mm});
            skLineSegment(sketch, "E772.MirrorCS", {"start": v(53.48, 15.7) * mm, "end": v(53.48, 17.2) * mm});
            skLineSegment(sketch, "E773.MirrorCS", {"start": v(89.48, 15.7) * mm, "end": v(89.48, 17.2) * mm});
            skLineSegment(sketch, "E774.MirrorCS", {"start": v(63.98, 21.2) * mm, "end": v(65.48, 21.2) * mm});
            skLineSegment(sketch, "E775.MirrorCS", {"start": v(53.48, 10.7) * mm, "end": v(53.48, 9.2) * mm});
            skLineSegment(sketch, "E776.MirrorCS", {"start": v(78.98, 21.2) * mm, "end": v(77.48, 21.2) * mm});
            skLineSegment(sketch, "E777.MirrorCS", {"start": v(83.98, 21.2) * mm, "end": v(85.48, 21.2) * mm});
            skLineSegment(sketch, "E778.MirrorCS", {"start": v(91.48, 10.7) * mm, "end": v(89.48, 10.7) * mm});
            skLineSegment(sketch, "E779.MirrorCS", {"start": v(63.98, 23.2) * mm, "end": v(63.98, 21.2) * mm});
            skLineSegment(sketch, "E780.MirrorCS", {"start": v(58.98, 23.2) * mm, "end": v(58.98, 21.2) * mm});
            skLineSegment(sketch, "E781.MirrorCS", {"start": v(91.48, 15.7) * mm, "end": v(89.48, 15.7) * mm});
            skLineSegment(sketch, "E782.MirrorCS", {"start": v(78.98, 23.2) * mm, "end": v(78.98, 21.2) * mm});
            skLineSegment(sketch, "E783.MirrorCS", {"start": v(83.98, 23.2) * mm, "end": v(83.98, 21.2) * mm});
            skLineSegment(sketch, "E784.MirrorCS", {"start": v(83.98, 5.2) * mm, "end": v(85.48, 5.2) * mm});
            skLineSegment(sketch, "E785.MirrorCS", {"start": v(69.48, 10.7) * mm, "end": v(69.48, 9.2) * mm});
            skLineSegment(sketch, "E786.MirrorCS", {"start": v(73.48, 10.7) * mm, "end": v(73.48, 9.2) * mm});
            skLineSegment(sketch, "E787.MirrorCS", {"start": v(73.48, 15.7) * mm, "end": v(73.48, 17.2) * mm});
            skLineSegment(sketch, "E788.MirrorCS", {"start": v(83.98, 3.2) * mm, "end": v(83.98, 5.2) * mm});
            skLineSegment(sketch, "E789.MirrorCS", {"start": v(63.98, 5.2) * mm, "end": v(65.48, 5.2) * mm});
            skLineSegment(sketch, "E790.MirrorCS", {"start": v(71.48, 10.7) * mm, "end": v(73.48, 10.7) * mm});
            skLineSegment(sketch, "E791.MirrorCS", {"start": v(71.48, 15.7) * mm, "end": v(69.48, 15.7) * mm});
            skLineSegment(sketch, "E792.MirrorCS", {"start": v(58.98, 5.2) * mm, "end": v(57.48, 5.2) * mm});
            skLineSegment(sketch, "E793.MirrorCS", {"start": v(71.48, 15.7) * mm, "end": v(73.48, 15.7) * mm});
            skLineSegment(sketch, "E794.MirrorCS", {"start": v(63.98, 3.2) * mm, "end": v(63.98, 5.2) * mm});
            skLineSegment(sketch, "E795.MirrorCS", {"start": v(78.98, 3.2) * mm, "end": v(78.98, 5.2) * mm});
            skLineSegment(sketch, "E796.MirrorCS", {"start": v(58.98, 3.2) * mm, "end": v(58.98, 5.2) * mm});
            skLineSegment(sketch, "E797.MirrorCS", {"start": v(78.98, 5.2) * mm, "end": v(77.48, 5.2) * mm});
            skLineSegment(sketch, "E798.MirrorCS", {"start": v(69.48, 15.7) * mm, "end": v(69.48, 17.2) * mm});
            skLineSegment(sketch, "E799.MirrorCS", {"start": v(71.48, 10.7) * mm, "end": v(69.48, 10.7) * mm});
            skLineSegment(sketch, "E800.MirrorCS", {"start": v(56.48, 13.2) * mm, "end": v(56.48, 17.2) * mm});
            skPoint(sketch, "E801.MirrorP", {"position": v(58.98, 21.2) * mm});
            skPoint(sketch, "E802.MirrorP", {"position": v(53.48, 13.2) * mm});
            skPoint(sketch, "E803.MirrorP", {"position": v(71.48, 23.2) * mm});
            skLineSegment(sketch, "E804.MirrorCS", {"start": v(57.48, 21.2) * mm, "end": v(57.48, 18.2) * mm});
            skPoint(sketch, "E805.MirrorP", {"position": v(91.48, 13.2) * mm});
            skLineSegment(sketch, "E806.MirrorCS", {"start": v(61.48, 18.2) * mm, "end": v(65.48, 18.2) * mm});
            skPoint(sketch, "E807.MirrorP", {"position": v(89.48, 13.2) * mm});
            skPoint(sketch, "E808.MirrorP", {"position": v(61.48, 23.2) * mm});
            skLineSegment(sketch, "E809.MirrorCS", {"start": v(53.48, 9.2) * mm, "end": v(56.48, 9.2) * mm});
            skPoint(sketch, "E810.MirrorP", {"position": v(61.48, 21.2) * mm});
            skPoint(sketch, "E811.MirrorP", {"position": v(89.48, 15.7) * mm});
            skLineSegment(sketch, "E812.MirrorCS", {"start": v(86.48, 13.2) * mm, "end": v(86.48, 17.2) * mm});
            skLineSegment(sketch, "E813.MirrorCS", {"start": v(89.48, 9.2) * mm, "end": v(86.48, 9.2) * mm});
            skPoint(sketch, "E814.MirrorP", {"position": v(81.48, 21.2) * mm});
            skLineSegment(sketch, "E815.MirrorCS", {"start": v(53.48, 17.2) * mm, "end": v(56.48, 17.2) * mm});
            skLineSegment(sketch, "E816.MirrorCS", {"start": v(85.48, 21.2) * mm, "end": v(85.48, 18.2) * mm});
            skPoint(sketch, "E817.MirrorP", {"position": v(53.48, 15.7) * mm});
            skPoint(sketch, "E818.MirrorP", {"position": v(81.48, 23.2) * mm});
            skLineSegment(sketch, "E819.MirrorCS", {"start": v(86.48, 13.2) * mm, "end": v(86.48, 9.2) * mm});
            skLineSegment(sketch, "E820.MirrorCS", {"start": v(61.48, 18.2) * mm, "end": v(57.48, 18.2) * mm});
            skLineSegment(sketch, "E821.MirrorCS", {"start": v(89.48, 17.2) * mm, "end": v(86.48, 17.2) * mm});
            skLineSegment(sketch, "E822.MirrorCS", {"start": v(56.48, 13.2) * mm, "end": v(56.48, 9.2) * mm});
            skLineSegment(sketch, "E823.MirrorCS", {"start": v(81.48, 18.2) * mm, "end": v(77.48, 18.2) * mm});
            skLineSegment(sketch, "E824.MirrorCS", {"start": v(77.48, 21.2) * mm, "end": v(77.48, 18.2) * mm});
            skLineSegment(sketch, "E825.MirrorCS", {"start": v(65.48, 21.2) * mm, "end": v(65.48, 18.2) * mm});
            skPoint(sketch, "E826.MirrorP", {"position": v(71.48, 13.2) * mm});
            skLineSegment(sketch, "E827.MirrorCS", {"start": v(81.48, 18.2) * mm, "end": v(85.48, 18.2) * mm});
            skPoint(sketch, "E828.MirrorP", {"position": v(83.98, 21.2) * mm});
            skPoint(sketch, "E829.MirrorP", {"position": v(73.48, 10.7) * mm});
            skLineSegment(sketch, "E830.MirrorCS", {"start": v(73.48, 9.2) * mm, "end": v(76.48, 9.2) * mm});
            skLineSegment(sketch, "E831.MirrorCS", {"start": v(69.48, 9.2) * mm, "end": v(66.48, 9.2) * mm});
            skLineSegment(sketch, "E832.MirrorCS", {"start": v(63.98, 3.2) * mm, "end": v(71.48, 3.2) * mm});
            skLineSegment(sketch, "E833.MirrorCS", {"start": v(91.48, 10.7) * mm, "end": v(91.48, 3.2) * mm});
            skLineSegment(sketch, "E834.MirrorCS", {"start": v(61.48, 8.2) * mm, "end": v(65.48, 8.2) * mm});
            skLineSegment(sketch, "E835.MirrorCS", {"start": v(66.48, 13.2) * mm, "end": v(66.48, 9.2) * mm});
            skPoint(sketch, "E836.MirrorP", {"position": v(73.48, 13.2) * mm});
            skPoint(sketch, "E837.MirrorP", {"position": v(91.48, 3.2) * mm});
            skLineSegment(sketch, "E838.MirrorCS", {"start": v(63.98, 23.2) * mm, "end": v(71.48, 23.2) * mm});
            skLineSegment(sketch, "E839.MirrorCS", {"start": v(85.48, 5.2) * mm, "end": v(85.48, 8.2) * mm});
            skLineSegment(sketch, "E840.MirrorCS", {"start": v(76.48, 13.2) * mm, "end": v(76.48, 17.2) * mm});
            skLineSegment(sketch, "E841.MirrorCS", {"start": v(69.48, 17.2) * mm, "end": v(66.48, 17.2) * mm});
            skLineSegment(sketch, "E842.MirrorCS", {"start": v(78.98, 3.2) * mm, "end": v(71.48, 3.2) * mm});
            skLineSegment(sketch, "E843.MirrorCS", {"start": v(73.48, 17.2) * mm, "end": v(76.48, 17.2) * mm});
            skPoint(sketch, "E844.MirrorP", {"position": v(69.48, 13.2) * mm});
            skPoint(sketch, "E845.MirrorP", {"position": v(69.48, 10.7) * mm});
            skLineSegment(sketch, "E846.MirrorCS", {"start": v(91.48, 23.2) * mm, "end": v(83.98, 23.2) * mm});
            skLineSegment(sketch, "E847.MirrorCS", {"start": v(91.48, 3.2) * mm, "end": v(83.98, 3.2) * mm});
            skLineSegment(sketch, "E848.MirrorCS", {"start": v(81.48, 8.2) * mm, "end": v(85.48, 8.2) * mm});
            skLineSegment(sketch, "E849.MirrorCS", {"start": v(91.48, 23.2) * mm, "end": v(91.48, 15.7) * mm});
            skLineSegment(sketch, "E850.MirrorCS", {"start": v(76.48, 13.2) * mm, "end": v(76.48, 9.2) * mm});
            skLineSegment(sketch, "E851.MirrorCS", {"start": v(81.48, 8.2) * mm, "end": v(77.48, 8.2) * mm});
            skCircle(sketch, "E852.MirrorC", {"center": v(81.48, 13.2) * mm, "radius": 2.5 * mm});
            skLineSegment(sketch, "E853.MirrorCS", {"start": v(61.48, 8.2) * mm, "end": v(57.48, 8.2) * mm});
            skLineSegment(sketch, "E854.MirrorCS", {"start": v(65.48, 5.2) * mm, "end": v(65.48, 8.2) * mm});
            skLineSegment(sketch, "E855.MirrorCS", {"start": v(66.48, 13.2) * mm, "end": v(66.48, 17.2) * mm});
            skCircle(sketch, "E856.MirrorC", {"center": v(61.48, 13.2) * mm, "radius": 2.5 * mm});
            skLineSegment(sketch, "E857.MirrorCS", {"start": v(77.48, 5.2) * mm, "end": v(77.48, 8.2) * mm});
            skLineSegment(sketch, "E858.MirrorCS", {"start": v(78.98, 23.2) * mm, "end": v(71.48, 23.2) * mm});
            skLineSegment(sketch, "E859.MirrorCS", {"start": v(57.48, 5.2) * mm, "end": v(57.48, 8.2) * mm});
            skSolve(sketch);
        }
        {
            var Q0;
            Q0 = qSketchRegion(id + "F10", true);
            extrude(context, id + "F11", {"entities" : qUnion([Q0]), "depth" : 500 * mm});
        }
    });
